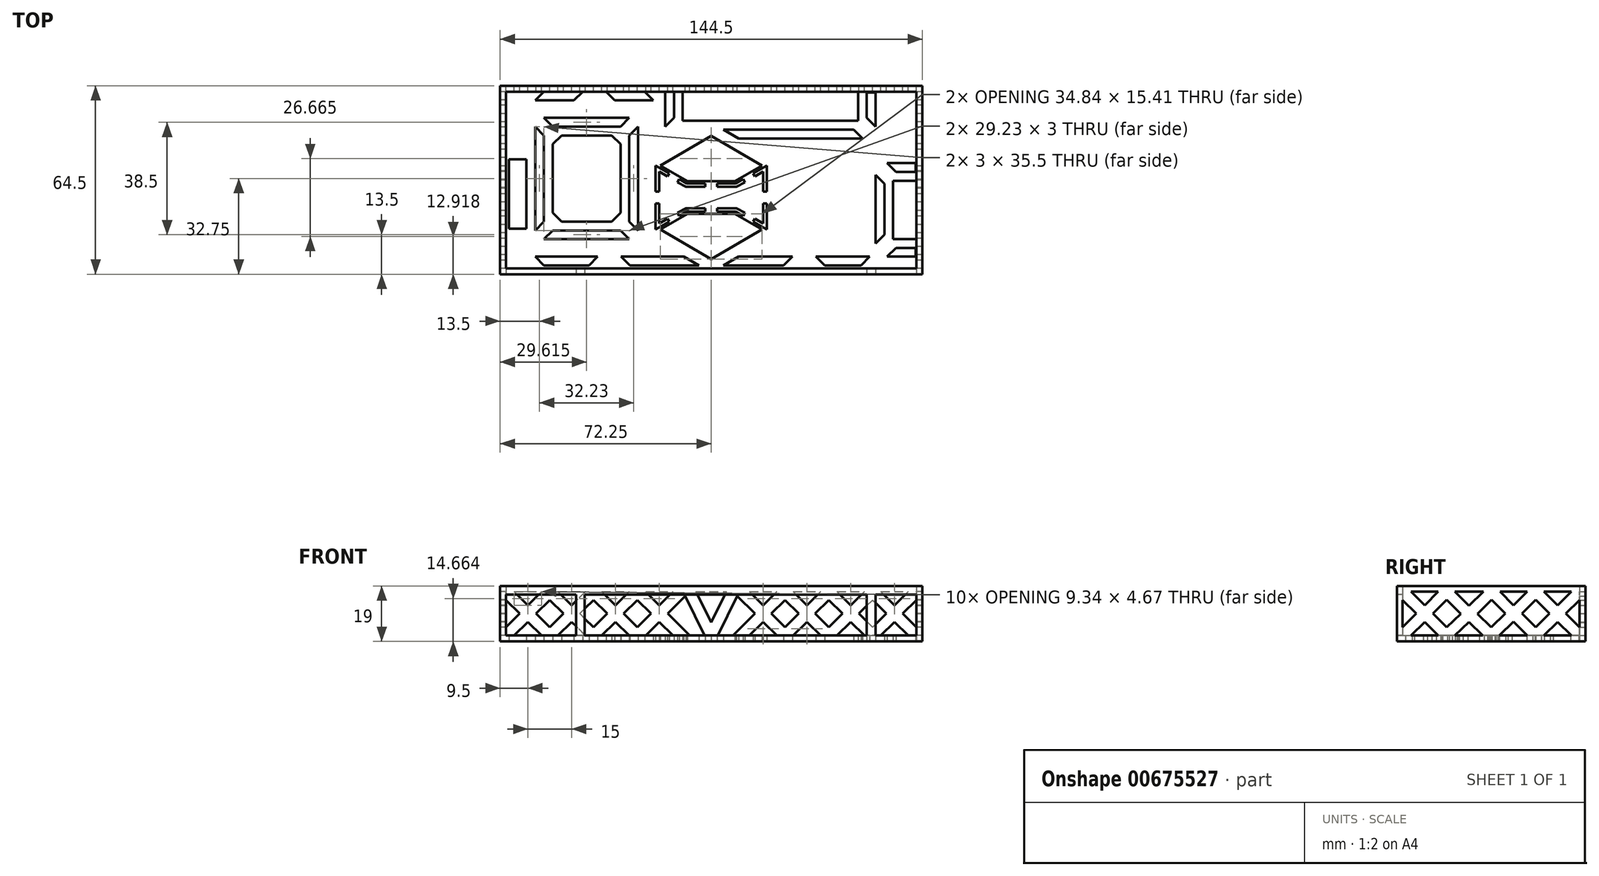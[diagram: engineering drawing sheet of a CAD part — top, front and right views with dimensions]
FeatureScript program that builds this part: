
annotation { "Feature Type Name" : "Feature", "Feature Type Description" : "" }
export const myFeature = defineFeature(function(context is Context, id is Id, definition is map)
    precondition{}
    {
        {
            var Q0;
            Q0=qCreatedBy(makeId("Top.planeOp"),FACE);
            var sketch = newSketch(context, id + "F0", { "sketchPlane" : qUnion([Q0])});
            skLineSegment(sketch, "E0.bottom", {"start": v(-72.25, 32.25) * mm, "end": v(72.25, 32.25) * mm});
            skLineSegment(sketch, "E0.top", {"start": v(-72.25, -32.25) * mm, "end": v(72.25, -32.25) * mm});
            skLineSegment(sketch, "E0.left", {"start": v(-72.25, 32.25) * mm, "end": v(-72.25, -32.25) * mm});
            skLineSegment(sketch, "E0.right", {"start": v(72.25, 32.25) * mm, "end": v(72.25, -32.25) * mm});
            skSolve(sketch);
        }
        {
            var Q0;
            Q0 = qSketchRegion(id + "F0", true);
            extrude(context, id + "F1", {"entities" : qUnion([Q0]), "depth" : 2 * mm, "offsetDistance" : 25 * mm});
        }
        {
            var Q0;
            Q0=makeQuery(id+"F1.opExtrude","CAP_FACE",FACE,{"disambiguationData":[OSD([sQuery(id+"F0.wireOp",EDGE,"E0.bottom"),sQuery(id+"F0.wireOp",EDGE,"E0.top"),sQuery(id+"F0.wireOp",EDGE,"E0.left"),sQuery(id+"F0.wireOp",EDGE,"E0.right")])],"isStart":false});
            var sketch = newSketch(context, id + "F2", { "sketchPlane" : qUnion([Q0])});
            skLineSegment(sketch, "E1.0", {"start": v(-72.25, 32.25) * mm, "end": v(-72.25, -32.25) * mm});
            skLineSegment(sketch, "E1.1", {"start": v(72.25, 32.25) * mm, "end": v(-72.25, 32.25) * mm});
            skLineSegment(sketch, "E1.2", {"start": v(72.25, -32.25) * mm, "end": v(72.25, 32.25) * mm});
            skLineSegment(sketch, "E1.3", {"start": v(-72.25, -32.25) * mm, "end": v(72.25, -32.25) * mm});
            skLineSegment(sketch, "E2.0", {"start": v(-70.25, 30.25) * mm, "end": v(-70.25, -30.25) * mm});
            skLineSegment(sketch, "E2.1", {"start": v(70.25, 30.25) * mm, "end": v(-70.25, 30.25) * mm});
            skLineSegment(sketch, "E2.2", {"start": v(70.25, -30.25) * mm, "end": v(70.25, 30.25) * mm});
            skLineSegment(sketch, "E2.3", {"start": v(-70.25, -30.25) * mm, "end": v(70.25, -30.25) * mm});
            skSolve(sketch);
        }
        {
            var Q0;
            Q0 = qSketchRegion(id + "F2", true);
            extrude(context, id + "F3", {"entities" : qUnion([Q0]), "operationType" : NewBodyOperationType.ADD, "depth" : 17 * mm, "offsetDistance" : 25 * mm});
        }
        {
            var Q0;
            Q0=makeQuery(id+"F3.boolean.opBoolean","MERGE",FACE,{"derivedFrom":[makeQuery(id+"F1.opExtrude","SWEPT_FACE",FACE,{"disambiguationData":[OSD([sQuery(id+"F0.wireOp",EDGE,"E0.top")])]}),makeQuery(id+"F3.opExtrude","SWEPT_FACE",FACE,{"disambiguationData":[OSD([sQuery(id+"F2.wireOp",EDGE,"E1.3")])]})]});
            var sketch = newSketch(context, id + "F4", { "sketchPlane" : qUnion([Q0])});
            skLineSegment(sketch, "E3.0", {"start": v(-70.25, 2) * mm, "end": v(-46.25, 2) * mm});
            skLineSegment(sketch, "E3.1", {"start": v(-70.25, 17) * mm, "end": v(-70.25, 2) * mm});
            skLineSegment(sketch, "E3.2", {"start": v(70.25, 17) * mm, "end": v(56.25, 17) * mm});
            skLineSegment(sketch, "E3.3", {"start": v(70.25, 2) * mm, "end": v(70.25, 17) * mm});
            skLineSegment(sketch, "E4", {"start": v(-46.25, 2) * mm, "end": v(-46.25, 17) * mm});
            skLineSegment(sketch, "E5", {"start": v(-44.25, 2) * mm, "end": v(-44.25, 17) * mm});
            skLineSegment(sketch, "E6", {"start": v(56.25, 2) * mm, "end": v(56.25, 17) * mm});
            skLineSegment(sketch, "E7", {"start": v(54.25, 2) * mm, "end": v(54.25, 17) * mm});
            skLineSegment(sketch, "E8.trimOffspring", {"start": v(54.25, 17) * mm, "end": v(-44.25, 17) * mm});
            skLineSegment(sketch, "E9.trimOffspring", {"start": v(56.25, 2) * mm, "end": v(70.25, 2) * mm});
            skLineSegment(sketch, "E10.trimOffspring", {"start": v(-46.25, 17) * mm, "end": v(-70.25, 17) * mm});
            skLineSegment(sketch, "E11.trimOffspring", {"start": v(-44.25, 2) * mm, "end": v(54.25, 2) * mm});
            skSolve(sketch);
        }
        {
            var Q0;
            Q0 = qSketchRegion(id + "F4", true);
            extrude(context, id + "F5", {"entities" : qUnion([Q0]), "operationType" : NewBodyOperationType.REMOVE, "oppositeDirection" : true, "depth" : 25 * mm, "offsetDistance" : 25 * mm});
        }
        {
            var Q0;
            Q0=makeQuery(id+"F1.opExtrude","CAP_FACE",FACE,{"disambiguationData":[OSD([sQuery(id+"F0.wireOp",EDGE,"E0.bottom"),sQuery(id+"F0.wireOp",EDGE,"E0.top"),sQuery(id+"F0.wireOp",EDGE,"E0.left"),sQuery(id+"F0.wireOp",EDGE,"E0.right")])],"isStart":true});
            var sketch = newSketch(context, id + "F6", { "sketchPlane" : qUnion([Q0])});
            skLineSegment(sketch, "E12.0", {"start": v(-70.25, 30.25) * mm, "end": v(-70.25, -30.25) * mm, "construction": true});
            skLineSegment(sketch, "E12.1", {"start": v(70.25, 30.25) * mm, "end": v(-70.25, 30.25) * mm, "construction": true});
            skLineSegment(sketch, "E12.3", {"start": v(-9.75, -30.25) * mm, "end": v(50.25, -30.25) * mm});
            skLineSegment(sketch, "E13", {"start": v(50.25, -30.25) * mm, "end": v(50.25, -20.25) * mm});
            skLineSegment(sketch, "E14", {"start": v(-9.75, -30.25) * mm, "end": v(-9.75, -20.25) * mm});
            skLineSegment(sketch, "E15", {"start": v(-9.75, -20.25) * mm, "end": v(50.25, -20.25) * mm});
            skLineSegment(sketch, "E16", {"start": v(50.25, -30.25) * mm, "end": v(70.25, -30.25) * mm, "construction": true});
            skLineSegment(sketch, "E17", {"start": v(-9.75, -30.25) * mm, "end": v(-70.25, -30.25) * mm, "construction": true});
            skLineSegment(sketch, "E18", {"start": v(70.25, 20.25) * mm, "end": v(62.25, 20.25) * mm});
            skLineSegment(sketch, "E19", {"start": v(70.25, 0.25) * mm, "end": v(62.25, 0.25) * mm});
            skLineSegment(sketch, "E20", {"start": v(70.25, -30.25) * mm, "end": v(70.25, 0.25) * mm, "construction": true});
            skLineSegment(sketch, "E21", {"start": v(70.25, 20.25) * mm, "end": v(70.25, 30.25) * mm, "construction": true});
            skLineSegment(sketch, "E22", {"start": v(70.25, 20.25) * mm, "end": v(70.25, 0.25) * mm});
            skLineSegment(sketch, "E23", {"start": v(62.25, 0.25) * mm, "end": v(62.25, 20.25) * mm});
            skSolve(sketch);
        }
        {
            var Q0;
            Q0 = qSketchRegion(id + "F6", true);
            extrude(context, id + "F7", {"entities" : qUnion([Q0]), "operationType" : NewBodyOperationType.REMOVE, "oppositeDirection" : true, "depth" : 25 * mm, "offsetDistance" : 25 * mm});
        }
        {
            var Q0;
            Q0=makeQuery(id+"F3.boolean.opBoolean","MERGE",FACE,{"derivedFrom":[makeQuery(id+"F1.opExtrude","SWEPT_FACE",FACE,{"disambiguationData":[OSD([sQuery(id+"F0.wireOp",EDGE,"E0.left")])]}),makeQuery(id+"F3.opExtrude","SWEPT_FACE",FACE,{"disambiguationData":[OSD([sQuery(id+"F2.wireOp",EDGE,"E1.0")])]})]});
            var sketch = newSketch(context, id + "F8", { "sketchPlane" : qUnion([Q0])});
            skLineSegment(sketch, "E24.0", {"start": v(-27.42, 2) * mm, "end": v(-18.08, 2) * mm});
            skLineSegment(sketch, "E24.1", {"start": v(-30.25, 14.17) * mm, "end": v(-30.25, 4.83) * mm});
            skLineSegment(sketch, "E24.3", {"start": v(30.25, 4.83) * mm, "end": v(30.25, 14.17) * mm});
            skLineSegment(sketch, "E25", {"start": v(-27.42, 17) * mm, "end": v(-18.08, 17) * mm});
            skLineSegment(sketch, "E26", {"start": v(-12.4, 17) * mm, "end": v(-3.08, 17) * mm});
            skLineSegment(sketch, "E27", {"start": v(2.63, 17) * mm, "end": v(12.4, 17) * mm});
            skLineSegment(sketch, "E28", {"start": v(18.08, 17) * mm, "end": v(27.42, 17) * mm});
            skLineSegment(sketch, "E29", {"start": v(-30.25, 2) * mm, "end": v(-15.25, 17) * mm, "construction": true});
            skLineSegment(sketch, "E30", {"start": v(-15.25, 17) * mm, "end": v(0, 2) * mm, "construction": true});
            skLineSegment(sketch, "E31", {"start": v(0, 2) * mm, "end": v(15.25, 17) * mm, "construction": true});
            skLineSegment(sketch, "E32", {"start": v(15.25, 17) * mm, "end": v(30.25, 2) * mm, "construction": true});
            skLineSegment(sketch, "E33", {"start": v(15.25, 17) * mm, "end": v(15.25, 2) * mm, "construction": true});
            skLineSegment(sketch, "E34", {"start": v(-0.25, 17) * mm, "end": v(0, 2) * mm, "construction": true});
            skLineSegment(sketch, "E35", {"start": v(-15.25, 17) * mm, "end": v(-15.25, 2) * mm, "construction": true});
            skLineSegment(sketch, "E36", {"start": v(-30.25, 17) * mm, "end": v(-15.25, 2) * mm, "construction": true});
            skLineSegment(sketch, "E37", {"start": v(-0.25, 17) * mm, "end": v(-15.25, 2) * mm, "construction": true});
            skLineSegment(sketch, "E38", {"start": v(30.25, 17) * mm, "end": v(15.25, 2) * mm, "construction": true});
            skLineSegment(sketch, "E39", {"start": v(-0.25, 17) * mm, "end": v(15.25, 2) * mm, "construction": true});
            skLineSegment(sketch, "E40.0", {"start": v(-27.42, 17) * mm, "end": v(-22.75, 12.33) * mm});
            skLineSegment(sketch, "E40.1", {"start": v(-3.08, 17) * mm, "end": v(-7.7, 12.38) * mm});
            skLineSegment(sketch, "E40.2", {"start": v(2.63, 17) * mm, "end": v(7.55, 12.23) * mm});
            skLineSegment(sketch, "E40.3", {"start": v(27.42, 17) * mm, "end": v(22.75, 12.33) * mm});
            skLineSegment(sketch, "E41.0", {"start": v(-30.25, 14.17) * mm, "end": v(-25.58, 9.5) * mm});
            skLineSegment(sketch, "E41.1", {"start": v(-0.23, 14.2) * mm, "end": v(-4.85, 9.57) * mm});
            skLineSegment(sketch, "E41.2", {"start": v(-0.23, 14.2) * mm, "end": v(4.7, 9.43) * mm});
            skLineSegment(sketch, "E41.3", {"start": v(30.25, 14.17) * mm, "end": v(18.08, 2) * mm});
            skLineSegment(sketch, "E42.0", {"start": v(15.24, 14.18) * mm, "end": v(19.92, 9.5) * mm});
            skLineSegment(sketch, "E42.1", {"start": v(2.85, 2) * mm, "end": v(7.57, 6.64) * mm});
            skLineSegment(sketch, "E42.2", {"start": v(-15.24, 14.18) * mm, "end": v(-10.53, 9.55) * mm});
            skLineSegment(sketch, "E42.3", {"start": v(-27.42, 2) * mm, "end": v(-22.75, 6.67) * mm});
            skLineSegment(sketch, "E43.0", {"start": v(18.08, 17) * mm, "end": v(22.75, 12.33) * mm});
            skLineSegment(sketch, "E43.1", {"start": v(0, 4.8) * mm, "end": v(4.7, 9.43) * mm});
            skLineSegment(sketch, "E43.2", {"start": v(-12.4, 17) * mm, "end": v(-7.7, 12.38) * mm});
            skLineSegment(sketch, "E43.3", {"start": v(-30.25, 4.83) * mm, "end": v(-25.58, 9.5) * mm});
            skLineSegment(sketch, "E44.trimOffspring", {"start": v(7.55, 12.23) * mm, "end": v(12.4, 17) * mm});
            skLineSegment(sketch, "E45.trimOffspring", {"start": v(7.57, 6.64) * mm, "end": v(12.37, 2) * mm});
            skLineSegment(sketch, "E46.trimOffspring", {"start": v(10.43, 9.45) * mm, "end": v(15.23, 4.8) * mm});
            skLineSegment(sketch, "E47.trimOffspring", {"start": v(22.75, 6.67) * mm, "end": v(27.42, 2) * mm});
            skLineSegment(sketch, "E48.trimOffspring", {"start": v(19.92, 9.5) * mm, "end": v(15.23, 4.8) * mm});
            skLineSegment(sketch, "E49.trimOffspring", {"start": v(25.58, 9.5) * mm, "end": v(30.25, 4.83) * mm});
            skLineSegment(sketch, "E50.trimOffspring", {"start": v(10.43, 9.45) * mm, "end": v(15.24, 14.18) * mm});
            skLineSegment(sketch, "E51.trimOffspring", {"start": v(-7.68, 6.75) * mm, "end": v(-2.85, 2) * mm});
            skLineSegment(sketch, "E52.trimOffspring", {"start": v(-7.68, 6.75) * mm, "end": v(-12.42, 2) * mm});
            skLineSegment(sketch, "E53.trimOffspring", {"start": v(-4.85, 9.57) * mm, "end": v(0, 4.8) * mm});
            skLineSegment(sketch, "E54.trimOffspring", {"start": v(-10.53, 9.55) * mm, "end": v(-15.25, 4.83) * mm});
            skLineSegment(sketch, "E55.trimOffspring", {"start": v(-19.92, 9.5) * mm, "end": v(-15.25, 4.83) * mm});
            skLineSegment(sketch, "E56.trimOffspring", {"start": v(-22.75, 12.33) * mm, "end": v(-18.08, 17) * mm});
            skLineSegment(sketch, "E57.trimOffspring", {"start": v(-22.75, 6.67) * mm, "end": v(-18.08, 2) * mm});
            skLineSegment(sketch, "E58.trimOffspring", {"start": v(-19.92, 9.5) * mm, "end": v(-15.24, 14.18) * mm});
            skLineSegment(sketch, "E59.trimOffspring", {"start": v(-12.42, 2) * mm, "end": v(-2.85, 2) * mm});
            skLineSegment(sketch, "E60.trimOffspring", {"start": v(2.85, 2) * mm, "end": v(12.37, 2) * mm});
            skLineSegment(sketch, "E61.trimOffspring", {"start": v(18.08, 2) * mm, "end": v(27.42, 2) * mm});
            skSolve(sketch);
        }
        {
            var Q0;
            Q0 = qSketchRegion(id + "F8", true);
            extrude(context, id + "F9", {"entities" : qUnion([Q0]), "operationType" : NewBodyOperationType.REMOVE, "endBound" : BoundingType.THROUGH_ALL, "oppositeDirection" : true, "depth" : 25 * mm, "offsetDistance" : 25 * mm});
        }
        {
            var Q0;
            Q0=makeQuery(id+"F3.boolean.opBoolean","MERGE",FACE,{"derivedFrom":[makeQuery(id+"F1.opExtrude","SWEPT_FACE",FACE,{"disambiguationData":[OSD([sQuery(id+"F0.wireOp",EDGE,"E0.bottom")])]}),makeQuery(id+"F3.opExtrude","SWEPT_FACE",FACE,{"disambiguationData":[OSD([sQuery(id+"F2.wireOp",EDGE,"E1.1")])]})]});
            var sketch = newSketch(context, id + "F10", { "sketchPlane" : qUnion([Q0])});
            skLineSegment(sketch, "E62.0", {"start": v(-67.42, 2) * mm, "end": v(-58.08, 2) * mm});
            skLineSegment(sketch, "E62.1", {"start": v(-70.25, 14.17) * mm, "end": v(-70.25, 4.83) * mm});
            skLineSegment(sketch, "E62.2", {"start": v(67.42, 17) * mm, "end": v(58.08, 17) * mm});
            skLineSegment(sketch, "E62.3", {"start": v(70.25, 4.83) * mm, "end": v(70.25, 14.17) * mm});
            skLineSegment(sketch, "E63", {"start": v(0, 17) * mm, "end": v(0, 2) * mm, "construction": true});
            skLineSegment(sketch, "E64", {"start": v(-70.25, 17) * mm, "end": v(-55.25, 2) * mm, "construction": true});
            skLineSegment(sketch, "E65", {"start": v(-55.25, 2) * mm, "end": v(-40.25, 17) * mm, "construction": true});
            skLineSegment(sketch, "E66", {"start": v(-40.25, 17) * mm, "end": v(-25.25, 2) * mm, "construction": true});
            skLineSegment(sketch, "E67", {"start": v(-25.25, 2) * mm, "end": v(-10.25, 17) * mm, "construction": true});
            skLineSegment(sketch, "E68", {"start": v(70.25, 17) * mm, "end": v(55.25, 2) * mm, "construction": true});
            skLineSegment(sketch, "E69", {"start": v(55.25, 2) * mm, "end": v(40.25, 17) * mm, "construction": true});
            skLineSegment(sketch, "E70", {"start": v(40.25, 17) * mm, "end": v(25.25, 2) * mm, "construction": true});
            skLineSegment(sketch, "E71", {"start": v(25.25, 2) * mm, "end": v(10.25, 17) * mm, "construction": true});
            skLineSegment(sketch, "E72", {"start": v(-70.25, 2) * mm, "end": v(-55.25, 17) * mm, "construction": true});
            skLineSegment(sketch, "E73", {"start": v(-55.25, 17) * mm, "end": v(-40.25, 2) * mm, "construction": true});
            skLineSegment(sketch, "E74", {"start": v(-40.25, 2) * mm, "end": v(-25.25, 17) * mm, "construction": true});
            skLineSegment(sketch, "E75", {"start": v(-25.25, 17) * mm, "end": v(-10.25, 2) * mm, "construction": true});
            skLineSegment(sketch, "E76", {"start": v(70.25, 2) * mm, "end": v(55.25, 17) * mm, "construction": true});
            skLineSegment(sketch, "E77", {"start": v(55.25, 17) * mm, "end": v(40.25, 2) * mm, "construction": true});
            skLineSegment(sketch, "E78", {"start": v(40.25, 2) * mm, "end": v(25.25, 17) * mm, "construction": true});
            skLineSegment(sketch, "E79", {"start": v(25.25, 17) * mm, "end": v(10.25, 2) * mm, "construction": true});
            skLineSegment(sketch, "E80.0", {"start": v(-22.42, 2) * mm, "end": v(-17.75, 6.67) * mm});
            skLineSegment(sketch, "E80.1", {"start": v(-40.25, 14.17) * mm, "end": v(-35.58, 9.5) * mm});
            skLineSegment(sketch, "E80.2", {"start": v(-52.42, 2) * mm, "end": v(-47.75, 6.67) * mm});
            skLineSegment(sketch, "E80.3", {"start": v(-70.25, 14.17) * mm, "end": v(-65.58, 9.5) * mm});
            skLineSegment(sketch, "E81.0", {"start": v(-25.25, 4.83) * mm, "end": v(-20.58, 9.5) * mm});
            skLineSegment(sketch, "E81.1", {"start": v(-37.42, 17) * mm, "end": v(-32.75, 12.33) * mm});
            skLineSegment(sketch, "E81.2", {"start": v(-55.25, 4.83) * mm, "end": v(-50.58, 9.5) * mm});
            skLineSegment(sketch, "E81.3", {"start": v(-67.42, 17) * mm, "end": v(-62.75, 12.33) * mm});
            skLineSegment(sketch, "E82.0", {"start": v(-25.25, 14.17) * mm, "end": v(-20.58, 9.5) * mm});
            skLineSegment(sketch, "E82.1", {"start": v(-37.42, 2) * mm, "end": v(-25.25, 14.17) * mm});
            skLineSegment(sketch, "E82.2", {"start": v(-55.25, 14.17) * mm, "end": v(-50.58, 9.5) * mm});
            skLineSegment(sketch, "E82.3", {"start": v(-67.42, 2) * mm, "end": v(-62.75, 6.67) * mm});
            skLineSegment(sketch, "E83.0", {"start": v(-22.42, 17) * mm, "end": v(-17.75, 12.33) * mm});
            skLineSegment(sketch, "E83.1", {"start": v(-40.25, 4.83) * mm, "end": v(-35.58, 9.5) * mm});
            skLineSegment(sketch, "E83.2", {"start": v(-52.42, 17) * mm, "end": v(-47.75, 12.33) * mm});
            skLineSegment(sketch, "E83.3", {"start": v(-70.25, 4.83) * mm, "end": v(-65.58, 9.5) * mm});
            skLineSegment(sketch, "E84.0", {"start": v(25.25, 4.83) * mm, "end": v(20.58, 9.5) * mm});
            skLineSegment(sketch, "E84.1", {"start": v(37.42, 17) * mm, "end": v(32.75, 12.33) * mm});
            skLineSegment(sketch, "E84.2", {"start": v(55.25, 4.83) * mm, "end": v(50.58, 9.5) * mm});
            skLineSegment(sketch, "E84.3", {"start": v(67.42, 17) * mm, "end": v(62.75, 12.33) * mm});
            skLineSegment(sketch, "E85.0", {"start": v(22.42, 2) * mm, "end": v(17.75, 6.67) * mm});
            skLineSegment(sketch, "E85.1", {"start": v(40.25, 14.17) * mm, "end": v(35.58, 9.5) * mm});
            skLineSegment(sketch, "E85.2", {"start": v(52.42, 2) * mm, "end": v(47.75, 6.67) * mm});
            skLineSegment(sketch, "E85.3", {"start": v(70.25, 14.17) * mm, "end": v(65.58, 9.5) * mm});
            skLineSegment(sketch, "E86.0", {"start": v(22.42, 17) * mm, "end": v(17.75, 12.33) * mm});
            skLineSegment(sketch, "E86.1", {"start": v(40.25, 4.83) * mm, "end": v(35.58, 9.5) * mm});
            skLineSegment(sketch, "E86.2", {"start": v(52.42, 17) * mm, "end": v(47.75, 12.33) * mm});
            skLineSegment(sketch, "E86.3", {"start": v(70.25, 4.83) * mm, "end": v(65.58, 9.5) * mm});
            skLineSegment(sketch, "E87.0", {"start": v(25.25, 14.17) * mm, "end": v(20.58, 9.5) * mm});
            skLineSegment(sketch, "E87.1", {"start": v(37.42, 2) * mm, "end": v(32.75, 6.67) * mm});
            skLineSegment(sketch, "E87.2", {"start": v(55.25, 14.17) * mm, "end": v(50.58, 9.5) * mm});
            skLineSegment(sketch, "E87.3", {"start": v(67.42, 2) * mm, "end": v(62.75, 6.67) * mm});
            skLineSegment(sketch, "E88.trimOffspring", {"start": v(-19.16, 8.09) * mm, "end": v(-13.08, 2) * mm});
            skLineSegment(sketch, "E89.trimOffspring", {"start": v(-17.75, 12.33) * mm, "end": v(-13.08, 17) * mm});
            skLineSegment(sketch, "E90.trimOffspring", {"start": v(-14.92, 9.5) * mm, "end": v(-7.42, 2) * mm});
            skLineSegment(sketch, "E91.trimOffspring", {"start": v(-14.92, 9.5) * mm, "end": v(-8.91, 15.5) * mm});
            skLineSegment(sketch, "E92.trimOffspring", {"start": v(-32.75, 6.67) * mm, "end": v(-28.08, 2) * mm});
            skLineSegment(sketch, "E93.trimOffspring", {"start": v(-32.75, 12.33) * mm, "end": v(-28.08, 17) * mm});
            skLineSegment(sketch, "E94.trimOffspring", {"start": v(-29.92, 9.5) * mm, "end": v(-25.25, 4.83) * mm});
            skLineSegment(sketch, "E95.trimOffspring", {"start": v(-47.75, 6.67) * mm, "end": v(-43.08, 2) * mm});
            skLineSegment(sketch, "E96.trimOffspring", {"start": v(-47.75, 12.33) * mm, "end": v(-43.08, 17) * mm});
            skLineSegment(sketch, "E97.trimOffspring", {"start": v(-44.92, 9.5) * mm, "end": v(-40.25, 4.83) * mm});
            skLineSegment(sketch, "E98.trimOffspring", {"start": v(-44.92, 9.5) * mm, "end": v(-40.25, 14.17) * mm});
            skLineSegment(sketch, "E99.trimOffspring", {"start": v(-59.92, 9.5) * mm, "end": v(-55.25, 4.83) * mm});
            skLineSegment(sketch, "E100.trimOffspring", {"start": v(-59.92, 9.5) * mm, "end": v(-55.25, 14.17) * mm});
            skLineSegment(sketch, "E101.trimOffspring", {"start": v(-62.75, 6.67) * mm, "end": v(-58.08, 2) * mm});
            skLineSegment(sketch, "E102.trimOffspring", {"start": v(-62.75, 12.33) * mm, "end": v(-58.08, 17) * mm});
            skLineSegment(sketch, "E103.trimOffspring", {"start": v(14.92, 9.5) * mm, "end": v(8.91, 15.5) * mm});
            skLineSegment(sketch, "E104.trimOffspring", {"start": v(17.75, 6.67) * mm, "end": v(13.08, 2) * mm});
            skLineSegment(sketch, "E105.trimOffspring", {"start": v(17.75, 12.33) * mm, "end": v(13.08, 17) * mm});
            skLineSegment(sketch, "E106.trimOffspring", {"start": v(14.92, 9.5) * mm, "end": v(7.42, 2) * mm});
            skLineSegment(sketch, "E107.trimOffspring", {"start": v(29.92, 9.5) * mm, "end": v(25.25, 14.17) * mm});
            skLineSegment(sketch, "E108.trimOffspring", {"start": v(32.75, 6.67) * mm, "end": v(28.08, 2) * mm});
            skLineSegment(sketch, "E109.trimOffspring", {"start": v(32.75, 12.33) * mm, "end": v(28.08, 17) * mm});
            skLineSegment(sketch, "E110.trimOffspring", {"start": v(29.92, 9.5) * mm, "end": v(25.25, 4.83) * mm});
            skLineSegment(sketch, "E111.trimOffspring", {"start": v(44.92, 9.5) * mm, "end": v(40.25, 14.17) * mm});
            skLineSegment(sketch, "E112.trimOffspring", {"start": v(47.75, 6.67) * mm, "end": v(43.08, 2) * mm});
            skLineSegment(sketch, "E113.trimOffspring", {"start": v(47.75, 12.33) * mm, "end": v(43.08, 17) * mm});
            skLineSegment(sketch, "E114.trimOffspring", {"start": v(44.92, 9.5) * mm, "end": v(40.25, 4.83) * mm});
            skLineSegment(sketch, "E115.trimOffspring", {"start": v(59.92, 9.5) * mm, "end": v(55.25, 4.83) * mm});
            skLineSegment(sketch, "E116.trimOffspring", {"start": v(62.75, 12.33) * mm, "end": v(58.08, 17) * mm});
            skLineSegment(sketch, "E117.trimOffspring", {"start": v(62.75, 6.67) * mm, "end": v(58.08, 2) * mm});
            skLineSegment(sketch, "E118.trimOffspring", {"start": v(59.92, 9.5) * mm, "end": v(55.25, 14.17) * mm});
            skLineSegment(sketch, "E119.trimOffspring", {"start": v(28.08, 2) * mm, "end": v(37.42, 2) * mm});
            skLineSegment(sketch, "E120.trimOffspring", {"start": v(13.08, 2) * mm, "end": v(22.42, 2) * mm});
            skLineSegment(sketch, "E121.trimOffspring", {"start": v(5.2, 17) * mm, "end": v(-5.2, 17) * mm});
            skLineSegment(sketch, "E122.trimOffspring", {"start": v(22.42, 17) * mm, "end": v(13.08, 17) * mm});
            skLineSegment(sketch, "E123.trimOffspring", {"start": v(37.42, 17) * mm, "end": v(28.08, 17) * mm});
            skLineSegment(sketch, "E124.trimOffspring", {"start": v(43.08, 2) * mm, "end": v(52.42, 2) * mm});
            skLineSegment(sketch, "E125.trimOffspring", {"start": v(58.08, 2) * mm, "end": v(67.42, 2) * mm});
            skLineSegment(sketch, "E126.trimOffspring", {"start": v(52.42, 17) * mm, "end": v(43.08, 17) * mm});
            skLineSegment(sketch, "E127.trimOffspring", {"start": v(-7.42, 2) * mm, "end": v(-2.23, 2) * mm});
            skLineSegment(sketch, "E128.trimOffspring", {"start": v(-22.42, 2) * mm, "end": v(-13.08, 2) * mm});
            skLineSegment(sketch, "E129.trimOffspring", {"start": v(-37.42, 2) * mm, "end": v(-28.08, 2) * mm});
            skLineSegment(sketch, "E130.trimOffspring", {"start": v(-52.42, 2) * mm, "end": v(-43.08, 2) * mm});
            skLineSegment(sketch, "E131.trimOffspring", {"start": v(-58.08, 17) * mm, "end": v(-67.42, 17) * mm});
            skLineSegment(sketch, "E132.trimOffspring", {"start": v(-43.08, 17) * mm, "end": v(-52.42, 17) * mm});
            skLineSegment(sketch, "E133.trimOffspring", {"start": v(-28.08, 17) * mm, "end": v(-37.42, 17) * mm});
            skLineSegment(sketch, "E134.trimOffspring", {"start": v(-13.08, 17) * mm, "end": v(-22.42, 17) * mm});
            skLineSegment(sketch, "E135", {"start": v(-7.42, 17) * mm, "end": v(0, 2) * mm, "construction": true});
            skLineSegment(sketch, "E136", {"start": v(7.42, 17) * mm, "end": v(0, 2) * mm, "construction": true});
            skLineSegment(sketch, "E137.0", {"start": v(5.2, 17) * mm, "end": v(0, 6.5) * mm});
            skLineSegment(sketch, "E137.1", {"start": v(-5.2, 17) * mm, "end": v(0, 6.5) * mm});
            skLineSegment(sketch, "E138.0", {"start": v(8.91, 15.5) * mm, "end": v(2.23, 2) * mm});
            skLineSegment(sketch, "E138.1", {"start": v(-8.91, 15.5) * mm, "end": v(-2.23, 2) * mm});
            skLineSegment(sketch, "E139.trimOffspring", {"start": v(2.23, 2) * mm, "end": v(7.42, 2) * mm});
            skSolve(sketch);
        }
        {
            var Q0;
            Q0 = qSketchRegion(id + "F10", true);
            extrude(context, id + "F11", {"entities" : qUnion([Q0]), "operationType" : NewBodyOperationType.REMOVE, "oppositeDirection" : true, "depth" : 25 * mm, "offsetDistance" : 25 * mm});
        }
        {
            var Q0;
            {var subQ0=sQuery(id+"F0.wireOp",EDGE,"E0.top");var subQ1=sQuery(id+"F0.wireOp",EDGE,"E0.right");var subQ2=sQuery(id+"F0.wireOp",EDGE,"E0.bottom");var subQ3=sQuery(id+"F0.wireOp",EDGE,"E0.left");Q0=makeQuery(id+"FJUS3B1TuTwB0FU_1.boolean.opBoolean","SPLIT",FACE,{"disambiguationData":[TD([makeQuery(id+"F1.opExtrude","SWEPT_FACE",FACE,{"disambiguationData":[OSD([subQ2])]})])],"derivedFrom":makeQuery(id+"F1.opExtrude","CAP_FACE",FACE,{"disambiguationData":[OSD([subQ2,subQ0,subQ3,subQ1])],"isStart":true})});}
            var sketch = newSketch(context, id + "F12", { "sketchPlane" : qUnion([Q0])});
            skLineSegment(sketch, "E140.1", {"start": v(9.5, 11.5) * mm, "end": v(9.5, 0.5) * mm});
            skLineSegment(sketch, "E140.4", {"start": v(-9.5, 0.5) * mm, "end": v(-9.5, 11.5) * mm});
            skLineSegment(sketch, "E141", {"start": v(-9.5, 11.5) * mm, "end": v(-4.18, 8.41) * mm});
            skLineSegment(sketch, "E142", {"start": v(9.5, 11.5) * mm, "end": v(4.18, 8.41) * mm});
            skLineSegment(sketch, "E143", {"start": v(-4.18, 3.59) * mm, "end": v(-9.5, 0.5) * mm});
            skLineSegment(sketch, "E144", {"start": v(4.18, 3.59) * mm, "end": v(9.5, 0.5) * mm});
            skLineSegment(sketch, "E145", {"start": v(-4.18, 3.59) * mm, "end": v(4.18, 3.59) * mm});
            skLineSegment(sketch, "E146", {"start": v(4.18, 8.41) * mm, "end": v(-4.18, 8.41) * mm});
            skLineSegment(sketch, "E147.0", {"start": v(4.07, 8.81) * mm, "end": v(-4.07, 8.81) * mm});
            skLineSegment(sketch, "E147.1", {"start": v(-8.7, 11.5) * mm, "end": v(-4.07, 8.81) * mm});
            skLineSegment(sketch, "E147.2", {"start": v(8.7, 11.5) * mm, "end": v(4.07, 8.81) * mm});
            skLineSegment(sketch, "E147.3", {"start": v(0, 16.52) * mm, "end": v(8.7, 11.5) * mm});
            skLineSegment(sketch, "E147.4", {"start": v(-8.7, 11.5) * mm, "end": v(0, 16.52) * mm});
            skLineSegment(sketch, "E148.0", {"start": v(0, -4.52) * mm, "end": v(-8.7, 0.5) * mm});
            skLineSegment(sketch, "E148.1", {"start": v(-4.07, 3.19) * mm, "end": v(-8.7, 0.5) * mm});
            skLineSegment(sketch, "E148.2", {"start": v(8.7, 0.5) * mm, "end": v(0, -4.52) * mm});
            skLineSegment(sketch, "E148.3", {"start": v(4.07, 3.19) * mm, "end": v(8.7, 0.5) * mm});
            skLineSegment(sketch, "E148.4", {"start": v(-4.07, 3.19) * mm, "end": v(4.07, 3.19) * mm});
            skLineSegment(sketch, "E149.0", {"start": v(-8.9, 1.55) * mm, "end": v(-8.9, 10.45) * mm});
            skLineSegment(sketch, "E149.1", {"start": v(-4.34, 4.19) * mm, "end": v(-8.9, 1.55) * mm});
            skLineSegment(sketch, "E149.2", {"start": v(-8.9, 10.45) * mm, "end": v(-4.34, 7.81) * mm});
            skLineSegment(sketch, "E149.3", {"start": v(-4.34, 4.19) * mm, "end": v(4.34, 4.19) * mm});
            skLineSegment(sketch, "E149.4", {"start": v(4.34, 7.81) * mm, "end": v(-4.34, 7.81) * mm});
            skLineSegment(sketch, "E149.5", {"start": v(8.9, 10.45) * mm, "end": v(4.34, 7.81) * mm});
            skLineSegment(sketch, "E149.6", {"start": v(8.9, 10.45) * mm, "end": v(8.9, 1.55) * mm});
            skLineSegment(sketch, "E149.7", {"start": v(4.34, 4.19) * mm, "end": v(8.9, 1.55) * mm});
            skLineSegment(sketch, "E150", {"start": v(9.5, 6) * mm, "end": v(8.9, 6) * mm, "construction": true});
            skLineSegment(sketch, "E151", {"start": v(8.9, 6) * mm, "end": v(-8.9, 6) * mm, "construction": true});
            skLineSegment(sketch, "E152", {"start": v(-8.9, 6) * mm, "end": v(-9.5, 6) * mm, "construction": true});
            skLineSegment(sketch, "E153", {"start": v(0, 16.52) * mm, "end": v(0, 8.81) * mm, "construction": true});
            skLineSegment(sketch, "E154", {"start": v(0, 8.81) * mm, "end": v(0, 8.41) * mm, "construction": true});
            skLineSegment(sketch, "E155", {"start": v(0, 8.41) * mm, "end": v(0, 7.81) * mm, "construction": true});
            skLineSegment(sketch, "E156", {"start": v(0, 7.81) * mm, "end": v(0, 4.19) * mm, "construction": true});
            skLineSegment(sketch, "E157", {"start": v(0, 4.19) * mm, "end": v(0, 3.59) * mm, "construction": true});
            skLineSegment(sketch, "E158", {"start": v(0, 3.59) * mm, "end": v(0, 3.19) * mm, "construction": true});
            skLineSegment(sketch, "E159", {"start": v(0, 3.19) * mm, "end": v(0, -4.52) * mm, "construction": true});
            skSolve(sketch);
        }
        {
            var Q0;
            Q0 = qSketchRegion(id + "F12", true);
            extrude(context, id + "F13", {"entities" : qUnion([Q0]), "depth" : 1 * mm, "offsetDistance" : 25 * mm});
        }
        {
            var Q0;
            Q0=makeQuery(id+"F13.opExtrude","CAP_FACE",FACE,{"disambiguationData":[OSD([sQuery(id+"F12.wireOp",EDGE,"E140.1"),sQuery(id+"F12.wireOp",EDGE,"E140.4"),sQuery(id+"F12.wireOp",EDGE,"E141"),sQuery(id+"F12.wireOp",EDGE,"E142"),sQuery(id+"F12.wireOp",EDGE,"E143"),sQuery(id+"F12.wireOp",EDGE,"E144"),sQuery(id+"F12.wireOp",EDGE,"E145"),sQuery(id+"F12.wireOp",EDGE,"E146"),sQuery(id+"F12.wireOp",EDGE,"E149.0"),sQuery(id+"F12.wireOp",EDGE,"E149.1"),sQuery(id+"F12.wireOp",EDGE,"E149.2"),sQuery(id+"F12.wireOp",EDGE,"E149.3"),sQuery(id+"F12.wireOp",EDGE,"E149.4"),sQuery(id+"F12.wireOp",EDGE,"E149.5"),sQuery(id+"F12.wireOp",EDGE,"E149.6"),sQuery(id+"F12.wireOp",EDGE,"E149.7")])],"isStart":false});
            var sketch = newSketch(context, id + "F14", { "sketchPlane" : qUnion([Q0])});
            skPoint(sketch, "E160", {"position": v(0, 6) * mm});
            skSolve(sketch);
        }
        {
            var Q0;
            Q0=makeQuery(id+"F13.opExtrude","SWEPT_BODY",BODY,{"disambiguationData":[OSD([sQuery(id+"F12.wireOp",EDGE,"E140.1"),sQuery(id+"F12.wireOp",EDGE,"E140.4"),sQuery(id+"F12.wireOp",EDGE,"E141"),sQuery(id+"F12.wireOp",EDGE,"E142"),sQuery(id+"F12.wireOp",EDGE,"E143"),sQuery(id+"F12.wireOp",EDGE,"E144"),sQuery(id+"F12.wireOp",EDGE,"E145"),sQuery(id+"F12.wireOp",EDGE,"E146"),sQuery(id+"F12.wireOp",EDGE,"E149.0"),sQuery(id+"F12.wireOp",EDGE,"E149.1"),sQuery(id+"F12.wireOp",EDGE,"E149.2"),sQuery(id+"F12.wireOp",EDGE,"E149.3"),sQuery(id+"F12.wireOp",EDGE,"E149.4"),sQuery(id+"F12.wireOp",EDGE,"E149.5"),sQuery(id+"F12.wireOp",EDGE,"E149.6"),sQuery(id+"F12.wireOp",EDGE,"E149.7")])]});
            var Q1;
            Q1=makeQuery(id+"F13.opExtrude","SWEPT_BODY",BODY,{"disambiguationData":[OSD([sQuery(id+"F12.wireOp",EDGE,"E147.0"),sQuery(id+"F12.wireOp",EDGE,"E147.1"),sQuery(id+"F12.wireOp",EDGE,"E147.2"),sQuery(id+"F12.wireOp",EDGE,"E147.3"),sQuery(id+"F12.wireOp",EDGE,"E147.4")])]});
            var Q2;
            Q2=makeQuery(id+"F13.opExtrude","SWEPT_BODY",BODY,{"disambiguationData":[OSD([sQuery(id+"F12.wireOp",EDGE,"E148.0"),sQuery(id+"F12.wireOp",EDGE,"E148.1"),sQuery(id+"F12.wireOp",EDGE,"E148.2"),sQuery(id+"F12.wireOp",EDGE,"E148.3"),sQuery(id+"F12.wireOp",EDGE,"E148.4")])]});
            var Q3;
            Q3=sQuery(id+"F14.wireOp",VERTEX,"E160");
            transform(context, id + "F15", {"entities" : qUnion([Q0, Q1, Q2]), "transformType" : TransformType.SCALE_UNIFORMLY, "scale" : 2, "scalePoint" : qUnion([Q3]), "makeCopy" : false});
        }
        {
            var Q0;
            Q0=makeQuery(id+"F13.opExtrude","CAP_FACE",FACE,{"disambiguationData":[OSD([sQuery(id+"F12.wireOp",EDGE,"E140.1"),sQuery(id+"F12.wireOp",EDGE,"E140.4"),sQuery(id+"F12.wireOp",EDGE,"E141"),sQuery(id+"F12.wireOp",EDGE,"E142"),sQuery(id+"F12.wireOp",EDGE,"E143"),sQuery(id+"F12.wireOp",EDGE,"E144"),sQuery(id+"F12.wireOp",EDGE,"E145"),sQuery(id+"F12.wireOp",EDGE,"E146"),sQuery(id+"F12.wireOp",EDGE,"E149.0"),sQuery(id+"F12.wireOp",EDGE,"E149.1"),sQuery(id+"F12.wireOp",EDGE,"E149.2"),sQuery(id+"F12.wireOp",EDGE,"E149.3"),sQuery(id+"F12.wireOp",EDGE,"E149.4"),sQuery(id+"F12.wireOp",EDGE,"E149.5"),sQuery(id+"F12.wireOp",EDGE,"E149.6"),sQuery(id+"F12.wireOp",EDGE,"E149.7")])],"isStart":false});
            var sketch = newSketch(context, id + "F16", { "sketchPlane" : qUnion([Q0])});
            skLineSegment(sketch, "E161.0", {"start": v(-8.36, 10.83) * mm, "end": v(-19.02, 16.98) * mm});
            skLineSegment(sketch, "E161.1", {"start": v(8.36, 10.83) * mm, "end": v(-8.36, 10.83) * mm});
            skLineSegment(sketch, "E161.2", {"start": v(-19.02, 16.98) * mm, "end": v(-19.02, -4.98) * mm});
            skLineSegment(sketch, "E161.3", {"start": v(19.02, 16.98) * mm, "end": v(8.36, 10.83) * mm});
            skLineSegment(sketch, "E161.4", {"start": v(-19.02, -4.98) * mm, "end": v(-8.36, 1.17) * mm});
            skLineSegment(sketch, "E161.5", {"start": v(-8.36, 1.17) * mm, "end": v(8.36, 1.17) * mm});
            skLineSegment(sketch, "E161.6", {"start": v(8.36, 1.17) * mm, "end": v(19.02, -4.98) * mm});
            skLineSegment(sketch, "E161.7", {"start": v(19.02, -4.98) * mm, "end": v(19.02, 16.98) * mm});
            skLineSegment(sketch, "E162.0", {"start": v(-8.68, 2.37) * mm, "end": v(-17.82, -2.9) * mm});
            skLineSegment(sketch, "E162.1", {"start": v(-8.68, 2.37) * mm, "end": v(8.68, 2.37) * mm});
            skLineSegment(sketch, "E162.2", {"start": v(-17.82, -2.9) * mm, "end": v(-17.82, 14.9) * mm});
            skLineSegment(sketch, "E162.3", {"start": v(8.68, 2.37) * mm, "end": v(17.82, -2.9) * mm});
            skLineSegment(sketch, "E162.4", {"start": v(-17.82, 14.9) * mm, "end": v(-8.68, 9.63) * mm});
            skLineSegment(sketch, "E162.5", {"start": v(8.68, 9.63) * mm, "end": v(-8.68, 9.63) * mm});
            skLineSegment(sketch, "E162.6", {"start": v(17.82, 14.9) * mm, "end": v(8.68, 9.63) * mm});
            skLineSegment(sketch, "E162.7", {"start": v(17.82, 14.9) * mm, "end": v(17.82, -2.9) * mm});
            skLineSegment(sketch, "E163.0", {"start": v(-17.42, 16.98) * mm, "end": v(-8.15, 11.63) * mm});
            skLineSegment(sketch, "E163.1", {"start": v(0, 27.04) * mm, "end": v(-17.42, 16.98) * mm});
            skLineSegment(sketch, "E163.2", {"start": v(-8.15, 11.63) * mm, "end": v(8.15, 11.63) * mm});
            skLineSegment(sketch, "E163.3", {"start": v(8.15, 11.63) * mm, "end": v(17.42, 16.98) * mm});
            skLineSegment(sketch, "E163.4", {"start": v(17.42, 16.98) * mm, "end": v(0, 27.04) * mm});
            skLineSegment(sketch, "E164.0", {"start": v(-8.15, 0.37) * mm, "end": v(-17.42, -4.98) * mm});
            skLineSegment(sketch, "E164.1", {"start": v(8.15, 0.37) * mm, "end": v(-8.15, 0.37) * mm});
            skLineSegment(sketch, "E164.2", {"start": v(-17.42, -4.98) * mm, "end": v(0, -15.04) * mm});
            skLineSegment(sketch, "E164.3", {"start": v(0, -15.04) * mm, "end": v(17.42, -4.98) * mm});
            skLineSegment(sketch, "E164.4", {"start": v(17.42, -4.98) * mm, "end": v(8.15, 0.37) * mm});
            skSolve(sketch);
        }
        {
            var Q0;
            Q0 = qSketchRegion(id + "F16", true);
            extrude(context, id + "F17", {"entities" : qUnion([Q0]), "operationType" : NewBodyOperationType.REMOVE, "oppositeDirection" : true, "depth" : 3 * mm, "offsetDistance" : 25 * mm});
        }
        {
            var Q0;
            Q0=makeQuery(id+"F17.boolean.opBoolean","SPLIT",FACE,{"disambiguationData":[TD([makeQuery(id+"F17.opExtrude","SWEPT_FACE",FACE,{"disambiguationData":[OSD([sQuery(id+"F16.wireOp",EDGE,"E162.0")])]})])],"derivedFrom":makeQuery(id+"F1.opExtrude","CAP_FACE",FACE,{"disambiguationData":[OSD([sQuery(id+"F0.wireOp",EDGE,"E0.bottom"),sQuery(id+"F0.wireOp",EDGE,"E0.top"),sQuery(id+"F0.wireOp",EDGE,"E0.left"),sQuery(id+"F0.wireOp",EDGE,"E0.right")])],"isStart":true})});
            var sketch = newSketch(context, id + "F18", { "sketchPlane" : qUnion([Q0])});
            skLineSegment(sketch, "E165.0", {"start": v(-2, 10.83) * mm, "end": v(2, 10.83) * mm});
            skLineSegment(sketch, "E165.1", {"start": v(14.38, 14.3) * mm, "end": v(10.92, 12.3) * mm});
            skLineSegment(sketch, "E165.2", {"start": v(-10.92, 12.3) * mm, "end": v(-14.38, 14.3) * mm});
            skLineSegment(sketch, "E165.3", {"start": v(19.02, 4) * mm, "end": v(19.02, 8) * mm});
            skLineSegment(sketch, "E165.4", {"start": v(-19.02, 4) * mm, "end": v(-19.02, 8) * mm});
            skLineSegment(sketch, "E165.5", {"start": v(-14.38, -2.3) * mm, "end": v(-10.92, -0.3) * mm});
            skLineSegment(sketch, "E165.6", {"start": v(2, 1.17) * mm, "end": v(-2, 1.17) * mm});
            skLineSegment(sketch, "E165.7", {"start": v(14.38, -2.3) * mm, "end": v(10.92, -0.3) * mm});
            skLineSegment(sketch, "E166.0", {"start": v(-2, 2.37) * mm, "end": v(2, 2.37) * mm});
            skLineSegment(sketch, "E166.1", {"start": v(-14.98, -1.26) * mm, "end": v(-11.52, 0.74) * mm});
            skLineSegment(sketch, "E166.2", {"start": v(11.52, 0.74) * mm, "end": v(14.98, -1.26) * mm});
            skLineSegment(sketch, "E166.3", {"start": v(-17.82, 8) * mm, "end": v(-17.82, 4) * mm});
            skLineSegment(sketch, "E166.4", {"start": v(17.82, 4) * mm, "end": v(17.82, 8) * mm});
            skLineSegment(sketch, "E166.5", {"start": v(14.98, 13.26) * mm, "end": v(11.52, 11.26) * mm});
            skLineSegment(sketch, "E166.6", {"start": v(2, 9.63) * mm, "end": v(-2, 9.63) * mm});
            skLineSegment(sketch, "E166.7", {"start": v(-11.52, 11.26) * mm, "end": v(-14.98, 13.26) * mm});
            skLineSegment(sketch, "E167", {"start": v(-17.82, 6) * mm, "end": v(-19.02, 6) * mm, "construction": true});
            skLineSegment(sketch, "E168", {"start": v(-17.82, 8) * mm, "end": v(-19.02, 8) * mm});
            skLineSegment(sketch, "E169", {"start": v(-17.82, 4) * mm, "end": v(-19.02, 4) * mm});
            skLineSegment(sketch, "E170", {"start": v(17.82, 6) * mm, "end": v(19.02, 6) * mm, "construction": true});
            skLineSegment(sketch, "E171", {"start": v(17.82, 8) * mm, "end": v(19.02, 8) * mm});
            skLineSegment(sketch, "E172", {"start": v(17.82, 4) * mm, "end": v(19.02, 4) * mm});
            skLineSegment(sketch, "E173", {"start": v(0, 9.63) * mm, "end": v(0, 10.83) * mm, "construction": true});
            skLineSegment(sketch, "E174", {"start": v(-13.25, -0.26) * mm, "end": v(-12.65, -1.3) * mm, "construction": true});
            skLineSegment(sketch, "E175", {"start": v(-13.25, 12.26) * mm, "end": v(-12.65, 13.3) * mm, "construction": true});
            skLineSegment(sketch, "E176", {"start": v(13.25, 12.26) * mm, "end": v(12.65, 13.3) * mm, "construction": true});
            skLineSegment(sketch, "E177", {"start": v(13.25, -0.26) * mm, "end": v(12.65, -1.3) * mm, "construction": true});
            skLineSegment(sketch, "E178", {"start": v(2, 1.17) * mm, "end": v(2, 2.37) * mm});
            skLineSegment(sketch, "E179", {"start": v(11.52, 0.74) * mm, "end": v(10.92, -0.3) * mm});
            skLineSegment(sketch, "E180", {"start": v(14.98, -1.26) * mm, "end": v(14.38, -2.3) * mm});
            skLineSegment(sketch, "E181", {"start": v(11.52, 11.26) * mm, "end": v(10.92, 12.3) * mm});
            skLineSegment(sketch, "E182", {"start": v(14.98, 13.26) * mm, "end": v(14.38, 14.3) * mm});
            skLineSegment(sketch, "E183", {"start": v(2, 9.63) * mm, "end": v(2, 10.83) * mm});
            skLineSegment(sketch, "E184", {"start": v(-2, 9.63) * mm, "end": v(-2, 10.83) * mm});
            skLineSegment(sketch, "E185", {"start": v(-11.52, 11.26) * mm, "end": v(-10.92, 12.3) * mm});
            skLineSegment(sketch, "E186", {"start": v(-14.98, 13.26) * mm, "end": v(-14.38, 14.3) * mm});
            skLineSegment(sketch, "E187", {"start": v(-11.52, 0.74) * mm, "end": v(-10.92, -0.3) * mm});
            skLineSegment(sketch, "E188", {"start": v(-14.98, -1.26) * mm, "end": v(-14.38, -2.3) * mm});
            skLineSegment(sketch, "E189", {"start": v(-2, 2.37) * mm, "end": v(-2, 1.17) * mm});
            skLineSegment(sketch, "E190", {"start": v(0, 2.37) * mm, "end": v(0, 1.17) * mm, "construction": true});
            skSolve(sketch);
        }
        {
            var Q0;
            Q0 = qSketchRegion(id + "F18", true);
            extrude(context, id + "F19", {"entities" : qUnion([Q0]), "oppositeDirection" : true, "depth" : 2 * mm, "offsetDistance" : 25 * mm});
        }
        {
            var Q0;
            Q0=makeQuery(id+"F17.boolean.opBoolean","SPLIT",BODY,{"disambiguationData":[OD(0.0)],"derivedFrom":makeQuery(id+"F1.opExtrude","SWEPT_BODY",BODY,{"disambiguationData":[OSD([sQuery(id+"F0.wireOp",EDGE,"E0.bottom"),sQuery(id+"F0.wireOp",EDGE,"E0.top"),sQuery(id+"F0.wireOp",EDGE,"E0.left"),sQuery(id+"F0.wireOp",EDGE,"E0.right")])]})});
            var Q1;
            Q1=makeQuery(id+"F17.boolean.opBoolean","SPLIT",BODY,{"disambiguationData":[OD(1.0)],"derivedFrom":makeQuery(id+"F1.opExtrude","SWEPT_BODY",BODY,{"disambiguationData":[OSD([sQuery(id+"F0.wireOp",EDGE,"E0.bottom"),sQuery(id+"F0.wireOp",EDGE,"E0.top"),sQuery(id+"F0.wireOp",EDGE,"E0.left"),sQuery(id+"F0.wireOp",EDGE,"E0.right")])]})});
            var Q2;
            Q2=makeQuery(id+"F19.opExtrude","SWEPT_BODY",BODY,{"disambiguationData":[OSD([sQuery(id+"F18.wireOp",EDGE,"E165.0"),sQuery(id+"F18.wireOp",EDGE,"E166.6"),sQuery(id+"F18.wireOp",EDGE,"E183"),sQuery(id+"F18.wireOp",EDGE,"E184")])]});
            var Q3;
            Q3=makeQuery(id+"F19.opExtrude","SWEPT_BODY",BODY,{"disambiguationData":[OSD([sQuery(id+"F18.wireOp",EDGE,"E165.1"),sQuery(id+"F18.wireOp",EDGE,"E166.5"),sQuery(id+"F18.wireOp",EDGE,"E181"),sQuery(id+"F18.wireOp",EDGE,"E182")])]});
            var Q4;
            Q4=makeQuery(id+"F19.opExtrude","SWEPT_BODY",BODY,{"disambiguationData":[OSD([sQuery(id+"F18.wireOp",EDGE,"E165.2"),sQuery(id+"F18.wireOp",EDGE,"E166.7"),sQuery(id+"F18.wireOp",EDGE,"E185"),sQuery(id+"F18.wireOp",EDGE,"E186")])]});
            var Q5;
            Q5=makeQuery(id+"F19.opExtrude","SWEPT_BODY",BODY,{"disambiguationData":[OSD([sQuery(id+"F18.wireOp",EDGE,"E165.3"),sQuery(id+"F18.wireOp",EDGE,"E166.4"),sQuery(id+"F18.wireOp",EDGE,"E171"),sQuery(id+"F18.wireOp",EDGE,"E172")])]});
            var Q6;
            Q6=makeQuery(id+"F19.opExtrude","SWEPT_BODY",BODY,{"disambiguationData":[OSD([sQuery(id+"F18.wireOp",EDGE,"E165.4"),sQuery(id+"F18.wireOp",EDGE,"E166.3"),sQuery(id+"F18.wireOp",EDGE,"E168"),sQuery(id+"F18.wireOp",EDGE,"E169")])]});
            var Q7;
            Q7=makeQuery(id+"F19.opExtrude","SWEPT_BODY",BODY,{"disambiguationData":[OSD([sQuery(id+"F18.wireOp",EDGE,"E165.5"),sQuery(id+"F18.wireOp",EDGE,"E166.1"),sQuery(id+"F18.wireOp",EDGE,"E187"),sQuery(id+"F18.wireOp",EDGE,"E188")])]});
            var Q8;
            Q8=makeQuery(id+"F19.opExtrude","SWEPT_BODY",BODY,{"disambiguationData":[OSD([sQuery(id+"F18.wireOp",EDGE,"E165.6"),sQuery(id+"F18.wireOp",EDGE,"E166.0"),sQuery(id+"F18.wireOp",EDGE,"E178"),sQuery(id+"F18.wireOp",EDGE,"E189")])]});
            var Q9;
            Q9=makeQuery(id+"F19.opExtrude","SWEPT_BODY",BODY,{"disambiguationData":[OSD([sQuery(id+"F18.wireOp",EDGE,"E165.7"),sQuery(id+"F18.wireOp",EDGE,"E166.2"),sQuery(id+"F18.wireOp",EDGE,"E179"),sQuery(id+"F18.wireOp",EDGE,"E180")])]});
            booleanBodies(context, id + "F20", {"operationType" : BooleanOperationType.UNION, "tools" : qUnion([Q0, Q1, Q2, Q3, Q4, Q5, Q6, Q7, Q8, Q9])});
        }
        {
            var Q0;
            {var subQ0=sQuery(id+"F0.wireOp",EDGE,"E0.top");var subQ1=sQuery(id+"F0.wireOp",EDGE,"E0.right");var subQ2=sQuery(id+"F0.wireOp",EDGE,"E0.bottom");var subQ3=sQuery(id+"F0.wireOp",EDGE,"E0.left");var subQ4=makeQuery(id+"F1.opExtrude","CAP_FACE",FACE,{"disambiguationData":[OSD([subQ2,subQ0,subQ3,subQ1])],"isStart":true});Q0=makeQuery(id+"F20.opBoolean","MERGE",FACE,{"derivedFrom":[makeQuery(id+"F17.boolean.opBoolean","SPLIT",FACE,{"disambiguationData":[TD([makeQuery(id+"F17.opExtrude","SWEPT_FACE",FACE,{"disambiguationData":[OSD([sQuery(id+"F16.wireOp",EDGE,"E162.0")])]})])],"derivedFrom":subQ4}),makeQuery(id+"F17.boolean.opBoolean","SPLIT",FACE,{"disambiguationData":[TD([makeQuery(id+"F1.opExtrude","SWEPT_FACE",FACE,{"disambiguationData":[OSD([subQ2])]})])],"derivedFrom":subQ4}),makeQuery(id+"F19.opExtrude","CAP_FACE",FACE,{"disambiguationData":[OSD([sQuery(id+"F18.wireOp",EDGE,"E165.0"),sQuery(id+"F18.wireOp",EDGE,"E166.6"),sQuery(id+"F18.wireOp",EDGE,"E183"),sQuery(id+"F18.wireOp",EDGE,"E184")])],"isStart":true}),makeQuery(id+"F19.opExtrude","CAP_FACE",FACE,{"disambiguationData":[OSD([sQuery(id+"F18.wireOp",EDGE,"E165.1"),sQuery(id+"F18.wireOp",EDGE,"E166.5"),sQuery(id+"F18.wireOp",EDGE,"E181"),sQuery(id+"F18.wireOp",EDGE,"E182")])],"isStart":true}),makeQuery(id+"F19.opExtrude","CAP_FACE",FACE,{"disambiguationData":[OSD([sQuery(id+"F18.wireOp",EDGE,"E165.2"),sQuery(id+"F18.wireOp",EDGE,"E166.7"),sQuery(id+"F18.wireOp",EDGE,"E185"),sQuery(id+"F18.wireOp",EDGE,"E186")])],"isStart":true}),makeQuery(id+"F19.opExtrude","CAP_FACE",FACE,{"disambiguationData":[OSD([sQuery(id+"F18.wireOp",EDGE,"E165.3"),sQuery(id+"F18.wireOp",EDGE,"E166.4"),sQuery(id+"F18.wireOp",EDGE,"E171"),sQuery(id+"F18.wireOp",EDGE,"E172")])],"isStart":true}),makeQuery(id+"F19.opExtrude","CAP_FACE",FACE,{"disambiguationData":[OSD([sQuery(id+"F18.wireOp",EDGE,"E165.4"),sQuery(id+"F18.wireOp",EDGE,"E166.3"),sQuery(id+"F18.wireOp",EDGE,"E168"),sQuery(id+"F18.wireOp",EDGE,"E169")])],"isStart":true}),makeQuery(id+"F19.opExtrude","CAP_FACE",FACE,{"disambiguationData":[OSD([sQuery(id+"F18.wireOp",EDGE,"E165.5"),sQuery(id+"F18.wireOp",EDGE,"E166.1"),sQuery(id+"F18.wireOp",EDGE,"E187"),sQuery(id+"F18.wireOp",EDGE,"E188")])],"isStart":true}),makeQuery(id+"F19.opExtrude","CAP_FACE",FACE,{"disambiguationData":[OSD([sQuery(id+"F18.wireOp",EDGE,"E165.6"),sQuery(id+"F18.wireOp",EDGE,"E166.0"),sQuery(id+"F18.wireOp",EDGE,"E178"),sQuery(id+"F18.wireOp",EDGE,"E189")])],"isStart":true}),makeQuery(id+"F19.opExtrude","CAP_FACE",FACE,{"disambiguationData":[OSD([sQuery(id+"F18.wireOp",EDGE,"E165.7"),sQuery(id+"F18.wireOp",EDGE,"E166.2"),sQuery(id+"F18.wireOp",EDGE,"E179"),sQuery(id+"F18.wireOp",EDGE,"E180")])],"isStart":true})]});}
            var sketch = newSketch(context, id + "F21", { "sketchPlane" : qUnion([Q0])});
            skLineSegment(sketch, "E191.0", {"start": v(70, 23.25) * mm, "end": v(63.24, 23.25) * mm});
            skLineSegment(sketch, "E191.1", {"start": v(59.25, 1.24) * mm, "end": v(59.25, 18.76) * mm});
            skLineSegment(sketch, "E191.2", {"start": v(70, -2.75) * mm, "end": v(63.24, -2.75) * mm});
            skLineSegment(sketch, "E192.0", {"start": v(70, -5.75) * mm, "end": v(60.24, -5.75) * mm});
            skLineSegment(sketch, "E192.1", {"start": v(56.25, -1.76) * mm, "end": v(56.25, 21.76) * mm});
            skLineSegment(sketch, "E192.2", {"start": v(70, 26.25) * mm, "end": v(60.24, 26.25) * mm});
            skLineSegment(sketch, "E193", {"start": v(70, 23.25) * mm, "end": v(70, 26.25) * mm});
            skLineSegment(sketch, "E194", {"start": v(70, -2.75) * mm, "end": v(70, -5.75) * mm});
            skLineSegment(sketch, "E195.0", {"start": v(59.25, 1.24) * mm, "end": v(56.25, -1.76) * mm});
            skLineSegment(sketch, "E196.0", {"start": v(63.24, -2.75) * mm, "end": v(60.24, -5.75) * mm});
            skLineSegment(sketch, "E197.0", {"start": v(63.24, 23.25) * mm, "end": v(60.24, 26.25) * mm});
            skLineSegment(sketch, "E198.0", {"start": v(59.25, 18.76) * mm, "end": v(56.25, 21.76) * mm});
            skLineSegment(sketch, "E199.0", {"start": v(53.25, -30) * mm, "end": v(53.25, -21.24) * mm});
            skLineSegment(sketch, "E199.1", {"start": v(-8.76, -17.25) * mm, "end": v(-4.17, -17.25) * mm});
            skLineSegment(sketch, "E199.2", {"start": v(-12.75, -30.25) * mm, "end": v(-12.75, -21.24) * mm});
            skLineSegment(sketch, "E200.0", {"start": v(56.25, -30) * mm, "end": v(56.25, -18.24) * mm});
            skLineSegment(sketch, "E200.1", {"start": v(-11.76, -14.25) * mm, "end": v(-9.37, -14.25) * mm});
            skLineSegment(sketch, "E200.2", {"start": v(-15.75, -30.25) * mm, "end": v(-15.75, -18.24) * mm});
            skLineSegment(sketch, "E201.0", {"start": v(-4.17, -17.25) * mm, "end": v(-9.37, -14.25) * mm});
            skLineSegment(sketch, "E201.1", {"start": v(9.37, -14.25) * mm, "end": v(4.17, -17.25) * mm});
            skLineSegment(sketch, "E202.0", {"start": v(53.25, -21.24) * mm, "end": v(56.25, -18.24) * mm});
            skLineSegment(sketch, "E203.0", {"start": v(48.76, -17.25) * mm, "end": v(51.76, -14.25) * mm});
            skLineSegment(sketch, "E204.0", {"start": v(-15.75, -18.24) * mm, "end": v(-12.75, -21.24) * mm});
            skLineSegment(sketch, "E205.0", {"start": v(-11.76, -14.25) * mm, "end": v(-8.76, -17.25) * mm});
            skLineSegment(sketch, "E206.trimOffspring", {"start": v(9.37, -14.25) * mm, "end": v(51.76, -14.25) * mm});
            skLineSegment(sketch, "E207.trimOffspring", {"start": v(4.17, -17.25) * mm, "end": v(48.76, -17.25) * mm});
            skLineSegment(sketch, "E208", {"start": v(-15.75, -30.25) * mm, "end": v(-12.75, -30.25) * mm});
            skLineSegment(sketch, "E209", {"start": v(53.25, -30) * mm, "end": v(56.25, -30) * mm});
            skLineSegment(sketch, "E210.0", {"start": v(-69.25, -27.25) * mm, "end": v(-69.25, -7.1) * mm});
            skLineSegment(sketch, "E211", {"start": v(-66, 0) * mm, "end": v(-69.25, 0) * mm, "construction": true});
            skLineSegment(sketch, "E212", {"start": v(-66.25, 4) * mm, "end": v(-69.25, 7) * mm});
            skLineSegment(sketch, "E213", {"start": v(-66.25, -4) * mm, "end": v(-69.25, -7.1) * mm});
            skLineSegment(sketch, "E214.trimOffspring", {"start": v(-69.25, 7) * mm, "end": v(-69.25, 26.25) * mm});
            skLineSegment(sketch, "E215.trimOffspring", {"start": v(-66.25, 4) * mm, "end": v(-66.25, 29.25) * mm});
            skLineSegment(sketch, "E216", {"start": v(-66.25, 29.25) * mm, "end": v(-69.25, 26.25) * mm});
            skPoint(sketch, "E217.orphan", {"position": v(-69.25, 32.21) * mm});
            skPoint(sketch, "E218.orphan", {"position": v(-66.25, 32) * mm});
            skLineSegment(sketch, "E219", {"start": v(-66.25, -30.25) * mm, "end": v(-66.25, -4) * mm});
            skLineSegment(sketch, "E220", {"start": v(-66.25, -30.25) * mm, "end": v(-69.25, -27.25) * mm});
            skPoint(sketch, "E221.orphan", {"position": v(-69.25, -32.21) * mm});
            skLineSegment(sketch, "E222", {"start": v(-57.25, -30.25) * mm, "end": v(-44, -30.25) * mm});
            skLineSegment(sketch, "E223", {"start": v(-19.75, -27.25) * mm, "end": v(-33, -27.25) * mm});
            skLineSegment(sketch, "E224", {"start": v(-60.25, -27.25) * mm, "end": v(-57.25, -30.25) * mm});
            skLineSegment(sketch, "E225", {"start": v(-19.75, -27.25) * mm, "end": v(-22.75, -30.25) * mm});
            skPoint(sketch, "E226.orphan", {"position": v(-15.75, -27.25) * mm});
            skPoint(sketch, "E227.orphan", {"position": v(-66.25, -27.25) * mm});
            skLineSegment(sketch, "E228", {"start": v(-40, -30.25) * mm, "end": v(-40, -27.25) * mm, "construction": true});
            skLineSegment(sketch, "E229", {"start": v(-44, -30.25) * mm, "end": v(-47, -27.25) * mm});
            skLineSegment(sketch, "E230", {"start": v(-36, -30.25) * mm, "end": v(-33, -27.25) * mm});
            skLineSegment(sketch, "E231.trimOffspring", {"start": v(-36, -30.25) * mm, "end": v(-22.75, -30.25) * mm});
            skLineSegment(sketch, "E232.trimOffspring", {"start": v(-47, -27.25) * mm, "end": v(-60.25, -27.25) * mm});
            skLineSegment(sketch, "E233", {"start": v(-57.25, 29.25) * mm, "end": v(-41.8, 29.25) * mm});
            skLineSegment(sketch, "E234.0", {"start": v(-9.37, 26.25) * mm, "end": v(-4.17, 29.25) * mm});
            skLineSegment(sketch, "E235", {"start": v(-60.25, 26.25) * mm, "end": v(-38.8, 26.25) * mm});
            skLineSegment(sketch, "E236", {"start": v(-60.25, 26.25) * mm, "end": v(-57.25, 29.25) * mm});
            skPoint(sketch, "E237.orphan", {"position": v(-66.25, 26.25) * mm});
            skLineSegment(sketch, "E238", {"start": v(9.37, 26.25) * mm, "end": v(27.8, 26.25) * mm});
            skLineSegment(sketch, "E239", {"start": v(4.17, 29.25) * mm, "end": v(24.8, 29.25) * mm});
            skLineSegment(sketch, "E240", {"start": v(54.24, 26.25) * mm, "end": v(51.24, 29.25) * mm});
            skPoint(sketch, "E241.start.orphan", {"position": v(70, 29.25) * mm});
            skLineSegment(sketch, "E242.0", {"start": v(4.17, 29.25) * mm, "end": v(9.37, 26.25) * mm});
            skLineSegment(sketch, "E243", {"start": v(31.8, 26.25) * mm, "end": v(31.8, 29.25) * mm, "construction": true});
            skLineSegment(sketch, "E244", {"start": v(27.8, 26.25) * mm, "end": v(24.8, 29.25) * mm});
            skLineSegment(sketch, "E245", {"start": v(35.8, 26.25) * mm, "end": v(38.8, 29.25) * mm});
            skLineSegment(sketch, "E246", {"start": v(-34.8, 26.25) * mm, "end": v(-34.8, 29.25) * mm, "construction": true});
            skLineSegment(sketch, "E247", {"start": v(-38.8, 26.25) * mm, "end": v(-41.8, 29.25) * mm});
            skLineSegment(sketch, "E248", {"start": v(-30.8, 26.25) * mm, "end": v(-27.8, 29.25) * mm});
            skLineSegment(sketch, "E249.trimOffspring", {"start": v(38.8, 29.25) * mm, "end": v(51.24, 29.25) * mm});
            skLineSegment(sketch, "E250.trimOffspring", {"start": v(35.8, 26.25) * mm, "end": v(54.24, 26.25) * mm});
            skLineSegment(sketch, "E251.trimOffspring", {"start": v(-30.8, 26.25) * mm, "end": v(-9.37, 26.25) * mm});
            skLineSegment(sketch, "E252.trimOffspring", {"start": v(-27.8, 29.25) * mm, "end": v(-4.17, 29.25) * mm});
            skLineSegment(sketch, "E253.bottom", {"start": v(-57.25, 20.25) * mm, "end": v(-28.02, 20.25) * mm});
            skLineSegment(sketch, "E253.left", {"start": v(-60.25, 17.25) * mm, "end": v(-60.25, -18.25) * mm});
            skLineSegment(sketch, "E253.right", {"start": v(-25.02, 17.25) * mm, "end": v(-25.02, -18.25) * mm});
            skLineSegment(sketch, "E254", {"start": v(-57.25, -21.25) * mm, "end": v(-28.02, -21.25) * mm});
            skLineSegment(sketch, "E255", {"start": v(-19.02, 16.98) * mm, "end": v(-19.02, 26.25) * mm, "construction": true});
            skLineSegment(sketch, "E256.0", {"start": v(-54.25, 17.25) * mm, "end": v(-31.02, 17.25) * mm});
            skLineSegment(sketch, "E256.1", {"start": v(-57.25, 14.25) * mm, "end": v(-57.25, -15.25) * mm});
            skLineSegment(sketch, "E256.2", {"start": v(-54.25, -18.25) * mm, "end": v(-31.02, -18.25) * mm});
            skLineSegment(sketch, "E256.3", {"start": v(-28.02, 14.25) * mm, "end": v(-28.02, -15.25) * mm});
            skLineSegment(sketch, "E257", {"start": v(-57.25, 20.25) * mm, "end": v(-54.25, 17.25) * mm});
            skLineSegment(sketch, "E258", {"start": v(-60.25, 17.25) * mm, "end": v(-57.25, 14.25) * mm});
            skLineSegment(sketch, "E259", {"start": v(-28.02, 20.25) * mm, "end": v(-31.02, 17.25) * mm});
            skLineSegment(sketch, "E260", {"start": v(-25.02, 17.25) * mm, "end": v(-28.02, 14.25) * mm});
            skLineSegment(sketch, "E261", {"start": v(-60.25, -18.25) * mm, "end": v(-57.25, -15.25) * mm});
            skLineSegment(sketch, "E262", {"start": v(-57.25, -21.25) * mm, "end": v(-54.25, -18.25) * mm});
            skLineSegment(sketch, "E263", {"start": v(-25.02, -18.25) * mm, "end": v(-28.02, -15.25) * mm});
            skLineSegment(sketch, "E264", {"start": v(-28.02, -21.25) * mm, "end": v(-31.02, -18.25) * mm});
            skLineSegment(sketch, "E265.0", {"start": v(-51.25, -15.25) * mm, "end": v(-34.02, -15.25) * mm});
            skLineSegment(sketch, "E265.1", {"start": v(-54.25, 11.25) * mm, "end": v(-54.25, -12.25) * mm});
            skLineSegment(sketch, "E265.2", {"start": v(-51.25, 14.25) * mm, "end": v(-34.02, 14.25) * mm});
            skLineSegment(sketch, "E265.3", {"start": v(-31.02, 11.25) * mm, "end": v(-31.02, -12.25) * mm});
            skLineSegment(sketch, "E266.0", {"start": v(-48.25, -12.25) * mm, "end": v(-37.02, -12.25) * mm});
            skLineSegment(sketch, "E266.1", {"start": v(-51.25, 8.25) * mm, "end": v(-51.25, -9.25) * mm});
            skLineSegment(sketch, "E266.2", {"start": v(-48.25, 11.25) * mm, "end": v(-37.02, 11.25) * mm});
            skLineSegment(sketch, "E266.3", {"start": v(-34.02, 8.25) * mm, "end": v(-34.02, -9.25) * mm});
            skLineSegment(sketch, "E267.0", {"start": v(-45.25, -9.25) * mm, "end": v(-40.02, -9.25) * mm});
            skLineSegment(sketch, "E267.1", {"start": v(-48.25, 5.25) * mm, "end": v(-48.25, 0.02) * mm});
            skLineSegment(sketch, "E267.2", {"start": v(-45.25, 8.25) * mm, "end": v(-40.02, 8.25) * mm});
            skLineSegment(sketch, "E267.3", {"start": v(-37.02, 5.25) * mm, "end": v(-37.02, 0.02) * mm});
            skPoint(sketch, "E268.orphan", {"position": v(-60.25, -21.25) * mm});
            skLineSegment(sketch, "E269.trimOffspring", {"start": v(-51.25, -15.25) * mm, "end": v(-48.25, -12.25) * mm});
            skLineSegment(sketch, "E270.trimOffspring", {"start": v(-54.25, -12.25) * mm, "end": v(-51.25, -9.25) * mm});
            skLineSegment(sketch, "E271.trimOffspring", {"start": v(-45.25, -9.25) * mm, "end": v(-42.63, -6.63) * mm});
            skLineSegment(sketch, "E272.trimOffspring", {"start": v(-34.02, -15.25) * mm, "end": v(-37.02, -12.25) * mm});
            skPoint(sketch, "E273.orphan", {"position": v(-25.02, -21.25) * mm});
            skLineSegment(sketch, "E274.trimOffspring", {"start": v(-31.02, -12.25) * mm, "end": v(-34.02, -9.25) * mm});
            skLineSegment(sketch, "E275.trimOffspring", {"start": v(-40.02, -9.25) * mm, "end": v(-42.63, -6.63) * mm});
            skLineSegment(sketch, "E276.trimOffspring", {"start": v(-31.02, 11.25) * mm, "end": v(-34.02, 8.25) * mm});
            skPoint(sketch, "E277.orphan", {"position": v(-25.02, 20.25) * mm});
            skLineSegment(sketch, "E278.trimOffspring", {"start": v(-34.02, 14.25) * mm, "end": v(-37.02, 11.25) * mm});
            skPoint(sketch, "E279.orphan", {"position": v(-60.25, 20.25) * mm});
            skLineSegment(sketch, "E280.trimOffspring", {"start": v(-51.25, 14.25) * mm, "end": v(-48.25, 11.25) * mm});
            skLineSegment(sketch, "E281.trimOffspring", {"start": v(-54.25, 11.25) * mm, "end": v(-51.25, 8.25) * mm});
            skLineSegment(sketch, "E282.trimOffspring", {"start": v(-48.25, 5.25) * mm, "end": v(-45.63, 2.63) * mm});
            skLineSegment(sketch, "E283.trimOffspring", {"start": v(-45.25, 8.25) * mm, "end": v(-42.63, 5.63) * mm});
            skLineSegment(sketch, "E284.trimOffspring", {"start": v(-40.02, 8.25) * mm, "end": v(-42.63, 5.63) * mm});
            skLineSegment(sketch, "E285.trimOffspring", {"start": v(-37.02, 5.25) * mm, "end": v(-39.63, 2.63) * mm});
            skLineSegment(sketch, "E286.trimOffspring", {"start": v(-45.5, -3.76) * mm, "end": v(-48.25, -1.02) * mm});
            skLineSegment(sketch, "E287.trimOffspring", {"start": v(-39.38, -3.38) * mm, "end": v(-37.02, -1.02) * mm});
            skLineSegment(sketch, "E288.trimOffspring", {"start": v(-37.02, -1.02) * mm, "end": v(-37.02, -5.75) * mm});
            skLineSegment(sketch, "E289", {"start": v(-37.02, -5.75) * mm, "end": v(-39.38, -3.38) * mm});
            skLineSegment(sketch, "E290.trimOffspring", {"start": v(-48.25, -1.02) * mm, "end": v(-48.25, -6.5) * mm});
            skLineSegment(sketch, "E291.trimOffspring", {"start": v(-45.63, 2.63) * mm, "end": v(-48.25, 0.02) * mm});
            skLineSegment(sketch, "E292.trimOffspring", {"start": v(-39.63, 2.63) * mm, "end": v(-37.02, 0.02) * mm});
            skLineSegment(sketch, "E293", {"start": v(-48.25, -6.5) * mm, "end": v(-45.5, -3.76) * mm});
            skSolve(sketch);
        }
        {
            var Q0;
            Q0 = qSketchRegion(id + "F21", true);
            extrude(context, id + "F22", {"entities" : qUnion([Q0]), "operationType" : NewBodyOperationType.REMOVE, "oppositeDirection" : true, "depth" : 25 * mm, "offsetDistance" : 25 * mm});
        }
        {
            var Q0;
            {var subQ0=sQuery(id+"F0.wireOp",EDGE,"E0.top");var subQ1=sQuery(id+"F0.wireOp",EDGE,"E0.right");var subQ2=sQuery(id+"F0.wireOp",EDGE,"E0.bottom");var subQ3=sQuery(id+"F0.wireOp",EDGE,"E0.left");var subQ4=makeQuery(id+"F1.opExtrude","CAP_FACE",FACE,{"disambiguationData":[OSD([subQ2,subQ0,subQ3,subQ1])],"isStart":true});Q0=makeQuery(id+"F20.opBoolean","MERGE",FACE,{"derivedFrom":[makeQuery(id+"F17.boolean.opBoolean","SPLIT",FACE,{"disambiguationData":[TD([makeQuery(id+"F17.opExtrude","SWEPT_FACE",FACE,{"disambiguationData":[OSD([sQuery(id+"F16.wireOp",EDGE,"E162.0")])]})])],"derivedFrom":subQ4}),makeQuery(id+"F17.boolean.opBoolean","SPLIT",FACE,{"disambiguationData":[TD([makeQuery(id+"F1.opExtrude","SWEPT_FACE",FACE,{"disambiguationData":[OSD([subQ2])]})])],"derivedFrom":subQ4}),makeQuery(id+"F19.opExtrude","CAP_FACE",FACE,{"disambiguationData":[OSD([sQuery(id+"F18.wireOp",EDGE,"E165.0"),sQuery(id+"F18.wireOp",EDGE,"E166.6"),sQuery(id+"F18.wireOp",EDGE,"E183"),sQuery(id+"F18.wireOp",EDGE,"E184")])],"isStart":true}),makeQuery(id+"F19.opExtrude","CAP_FACE",FACE,{"disambiguationData":[OSD([sQuery(id+"F18.wireOp",EDGE,"E165.1"),sQuery(id+"F18.wireOp",EDGE,"E166.5"),sQuery(id+"F18.wireOp",EDGE,"E181"),sQuery(id+"F18.wireOp",EDGE,"E182")])],"isStart":true}),makeQuery(id+"F19.opExtrude","CAP_FACE",FACE,{"disambiguationData":[OSD([sQuery(id+"F18.wireOp",EDGE,"E165.2"),sQuery(id+"F18.wireOp",EDGE,"E166.7"),sQuery(id+"F18.wireOp",EDGE,"E185"),sQuery(id+"F18.wireOp",EDGE,"E186")])],"isStart":true}),makeQuery(id+"F19.opExtrude","CAP_FACE",FACE,{"disambiguationData":[OSD([sQuery(id+"F18.wireOp",EDGE,"E165.3"),sQuery(id+"F18.wireOp",EDGE,"E166.4"),sQuery(id+"F18.wireOp",EDGE,"E171"),sQuery(id+"F18.wireOp",EDGE,"E172")])],"isStart":true}),makeQuery(id+"F19.opExtrude","CAP_FACE",FACE,{"disambiguationData":[OSD([sQuery(id+"F18.wireOp",EDGE,"E165.4"),sQuery(id+"F18.wireOp",EDGE,"E166.3"),sQuery(id+"F18.wireOp",EDGE,"E168"),sQuery(id+"F18.wireOp",EDGE,"E169")])],"isStart":true}),makeQuery(id+"F19.opExtrude","CAP_FACE",FACE,{"disambiguationData":[OSD([sQuery(id+"F18.wireOp",EDGE,"E165.5"),sQuery(id+"F18.wireOp",EDGE,"E166.1"),sQuery(id+"F18.wireOp",EDGE,"E187"),sQuery(id+"F18.wireOp",EDGE,"E188")])],"isStart":true}),makeQuery(id+"F19.opExtrude","CAP_FACE",FACE,{"disambiguationData":[OSD([sQuery(id+"F18.wireOp",EDGE,"E165.6"),sQuery(id+"F18.wireOp",EDGE,"E166.0"),sQuery(id+"F18.wireOp",EDGE,"E178"),sQuery(id+"F18.wireOp",EDGE,"E189")])],"isStart":true}),makeQuery(id+"F19.opExtrude","CAP_FACE",FACE,{"disambiguationData":[OSD([sQuery(id+"F18.wireOp",EDGE,"E165.7"),sQuery(id+"F18.wireOp",EDGE,"E166.2"),sQuery(id+"F18.wireOp",EDGE,"E179"),sQuery(id+"F18.wireOp",EDGE,"E180")])],"isStart":true})]});}
            var sketch = newSketch(context, id + "F23", { "sketchPlane" : qUnion([Q0])});
            skLineSegment(sketch, "E294", {"start": v(-69.25, -7.1) * mm, "end": v(-69.25, 16.62) * mm});
            skLineSegment(sketch, "E295", {"start": v(-69.25, 16.62) * mm, "end": v(-63.25, 16.62) * mm});
            skPoint(sketch, "E295.endSnap0", {"position": v(-66.25, 16.62) * mm});
            skLineSegment(sketch, "E296", {"start": v(-63.25, 16.62) * mm, "end": v(-63.25, -7.1) * mm});
            skLineSegment(sketch, "E297", {"start": v(-69.25, -7.1) * mm, "end": v(-63.25, -7.1) * mm});
            skSolve(sketch);
        }
        {
            var Q0;
            Q0 = qSketchRegion(id + "F23", true);
            extrude(context, id + "F24", {"entities" : qUnion([Q0]), "operationType" : NewBodyOperationType.REMOVE, "oppositeDirection" : true, "depth" : 25 * mm, "offsetDistance" : 25 * mm});
        }
        {
            var Q0;
            {var subQ0=sQuery(id+"F0.wireOp",EDGE,"E0.top");var subQ1=sQuery(id+"F0.wireOp",EDGE,"E0.right");var subQ2=sQuery(id+"F0.wireOp",EDGE,"E0.bottom");var subQ3=sQuery(id+"F0.wireOp",EDGE,"E0.left");var subQ4=makeQuery(id+"F1.opExtrude","CAP_FACE",FACE,{"disambiguationData":[OSD([subQ2,subQ0,subQ3,subQ1])],"isStart":true});Q0=makeQuery(id+"F20.opBoolean","MERGE",FACE,{"derivedFrom":[makeQuery(id+"F17.boolean.opBoolean","SPLIT",FACE,{"disambiguationData":[TD([makeQuery(id+"F17.opExtrude","SWEPT_FACE",FACE,{"disambiguationData":[OSD([sQuery(id+"F16.wireOp",EDGE,"E162.0")])]})])],"derivedFrom":subQ4}),makeQuery(id+"F17.boolean.opBoolean","SPLIT",FACE,{"disambiguationData":[TD([makeQuery(id+"F1.opExtrude","SWEPT_FACE",FACE,{"disambiguationData":[OSD([subQ2])]})])],"derivedFrom":subQ4}),makeQuery(id+"F19.opExtrude","CAP_FACE",FACE,{"disambiguationData":[OSD([sQuery(id+"F18.wireOp",EDGE,"E165.0"),sQuery(id+"F18.wireOp",EDGE,"E166.6"),sQuery(id+"F18.wireOp",EDGE,"E183"),sQuery(id+"F18.wireOp",EDGE,"E184")])],"isStart":true}),makeQuery(id+"F19.opExtrude","CAP_FACE",FACE,{"disambiguationData":[OSD([sQuery(id+"F18.wireOp",EDGE,"E165.1"),sQuery(id+"F18.wireOp",EDGE,"E166.5"),sQuery(id+"F18.wireOp",EDGE,"E181"),sQuery(id+"F18.wireOp",EDGE,"E182")])],"isStart":true}),makeQuery(id+"F19.opExtrude","CAP_FACE",FACE,{"disambiguationData":[OSD([sQuery(id+"F18.wireOp",EDGE,"E165.2"),sQuery(id+"F18.wireOp",EDGE,"E166.7"),sQuery(id+"F18.wireOp",EDGE,"E185"),sQuery(id+"F18.wireOp",EDGE,"E186")])],"isStart":true}),makeQuery(id+"F19.opExtrude","CAP_FACE",FACE,{"disambiguationData":[OSD([sQuery(id+"F18.wireOp",EDGE,"E165.3"),sQuery(id+"F18.wireOp",EDGE,"E166.4"),sQuery(id+"F18.wireOp",EDGE,"E171"),sQuery(id+"F18.wireOp",EDGE,"E172")])],"isStart":true}),makeQuery(id+"F19.opExtrude","CAP_FACE",FACE,{"disambiguationData":[OSD([sQuery(id+"F18.wireOp",EDGE,"E165.4"),sQuery(id+"F18.wireOp",EDGE,"E166.3"),sQuery(id+"F18.wireOp",EDGE,"E168"),sQuery(id+"F18.wireOp",EDGE,"E169")])],"isStart":true}),makeQuery(id+"F19.opExtrude","CAP_FACE",FACE,{"disambiguationData":[OSD([sQuery(id+"F18.wireOp",EDGE,"E165.5"),sQuery(id+"F18.wireOp",EDGE,"E166.1"),sQuery(id+"F18.wireOp",EDGE,"E187"),sQuery(id+"F18.wireOp",EDGE,"E188")])],"isStart":true}),makeQuery(id+"F19.opExtrude","CAP_FACE",FACE,{"disambiguationData":[OSD([sQuery(id+"F18.wireOp",EDGE,"E165.6"),sQuery(id+"F18.wireOp",EDGE,"E166.0"),sQuery(id+"F18.wireOp",EDGE,"E178"),sQuery(id+"F18.wireOp",EDGE,"E189")])],"isStart":true}),makeQuery(id+"F19.opExtrude","CAP_FACE",FACE,{"disambiguationData":[OSD([sQuery(id+"F18.wireOp",EDGE,"E165.7"),sQuery(id+"F18.wireOp",EDGE,"E166.2"),sQuery(id+"F18.wireOp",EDGE,"E179"),sQuery(id+"F18.wireOp",EDGE,"E180")])],"isStart":true})]});}
            var sketch = newSketch(context, id + "F25", { "sketchPlane" : qUnion([Q0])});
            skLineSegment(sketch, "E298", {"start": v(-69.25, -27.25) * mm, "end": v(-69.25, -7.1) * mm});
            skLineSegment(sketch, "E299", {"start": v(-66.25, -7.1) * mm, "end": v(-69.25, -7.1) * mm});
            skLineSegment(sketch, "E300", {"start": v(-66.25, -7.1) * mm, "end": v(-66.25, -30.25) * mm});
            skLineSegment(sketch, "E301", {"start": v(-66.25, 16.62) * mm, "end": v(-69.25, 16.62) * mm});
            skLineSegment(sketch, "E302", {"start": v(-69.25, 16.62) * mm, "end": v(-69.25, 26.25) * mm});
            skLineSegment(sketch, "E303", {"start": v(-66.25, 16.62) * mm, "end": v(-66.25, 29.25) * mm});
            skLineSegment(sketch, "E304", {"start": v(-69.25, -27.25) * mm, "end": v(-66.25, -30.25) * mm});
            skLineSegment(sketch, "E305", {"start": v(-69.25, 26.25) * mm, "end": v(-66.25, 29.25) * mm});
            skLineSegment(sketch, "E306", {"start": v(-39.38, -3.38) * mm, "end": v(-37.02, -5.75) * mm});
            skLineSegment(sketch, "E307", {"start": v(-37.02, -5.75) * mm, "end": v(-37.02, -1.02) * mm});
            skLineSegment(sketch, "E308", {"start": v(-37.02, -1.02) * mm, "end": v(-39.38, -3.38) * mm});
            skLineSegment(sketch, "E309", {"start": v(-40.02, -9.25) * mm, "end": v(-42.63, -6.63) * mm});
            skLineSegment(sketch, "E310", {"start": v(-42.63, -6.63) * mm, "end": v(-45.25, -9.25) * mm});
            skLineSegment(sketch, "E311", {"start": v(-45.25, -9.25) * mm, "end": v(-40.02, -9.25) * mm});
            skLineSegment(sketch, "E312", {"start": v(-48.25, -6.5) * mm, "end": v(-45.5, -3.76) * mm});
            skLineSegment(sketch, "E313", {"start": v(-45.5, -3.76) * mm, "end": v(-48.25, -1.02) * mm});
            skLineSegment(sketch, "E314", {"start": v(-48.25, -1.02) * mm, "end": v(-48.25, -6.5) * mm});
            skLineSegment(sketch, "E315", {"start": v(-48.25, 0.02) * mm, "end": v(-45.63, 2.63) * mm});
            skLineSegment(sketch, "E316", {"start": v(-45.63, 2.63) * mm, "end": v(-48.25, 5.25) * mm});
            skLineSegment(sketch, "E317", {"start": v(-48.25, 5.25) * mm, "end": v(-48.25, 0.02) * mm});
            skLineSegment(sketch, "E318", {"start": v(-42.63, 5.63) * mm, "end": v(-40.02, 8.25) * mm});
            skLineSegment(sketch, "E319", {"start": v(-40.02, 8.25) * mm, "end": v(-45.25, 8.25) * mm});
            skLineSegment(sketch, "E320", {"start": v(-45.25, 8.25) * mm, "end": v(-42.63, 5.63) * mm});
            skLineSegment(sketch, "E321", {"start": v(-39.63, 2.63) * mm, "end": v(-37.02, 0.02) * mm});
            skLineSegment(sketch, "E322", {"start": v(-37.02, 0.02) * mm, "end": v(-37.02, 5.25) * mm});
            skLineSegment(sketch, "E323", {"start": v(-37.02, 5.25) * mm, "end": v(-39.63, 2.63) * mm});
            skLineSegment(sketch, "E324", {"start": v(-4.17, -17.25) * mm, "end": v(-9.37, -14.25) * mm});
            skLineSegment(sketch, "E325", {"start": v(-9.37, -14.25) * mm, "end": v(-11.76, -14.25) * mm});
            skLineSegment(sketch, "E326", {"start": v(-11.76, -14.25) * mm, "end": v(-8.76, -17.25) * mm});
            skLineSegment(sketch, "E327", {"start": v(-8.76, -17.25) * mm, "end": v(-4.17, -17.25) * mm});
            skSolve(sketch);
        }
        {
            var Q0;
            Q0 = qSketchRegion(id + "F25", true);
            extrude(context, id + "F26", {"entities" : qUnion([Q0]), "operationType" : NewBodyOperationType.ADD, "oppositeDirection" : true, "depth" : 2 * mm, "offsetDistance" : 25 * mm});
        }
        {
            var Q0;
            Q0=makeQuery(id+"F5.boolean.opBoolean","COPY",FACE,{"derivedFrom":makeQuery(id+"F5.opExtrude","SWEPT_FACE",FACE,{"disambiguationData":[OSD([sQuery(id+"F4.wireOp",EDGE,"E7")])]})});
            var sketch = newSketch(context, id + "F27", { "sketchPlane" : qUnion([Q0])});
            skLineSegment(sketch, "E328.0", {"start": v(30.25, 17) * mm, "end": v(30.25, 2) * mm});
            skLineSegment(sketch, "E328.1", {"start": v(32.25, 17) * mm, "end": v(30.25, 17) * mm});
            skLineSegment(sketch, "E328.2", {"start": v(32.25, 2) * mm, "end": v(32.25, 17) * mm});
            skLineSegment(sketch, "E328.3", {"start": v(30.25, 2) * mm, "end": v(32.25, 2) * mm});
            skSolve(sketch);
        }
        {
            var Q0;
            Q0 = qSketchRegion(id + "F27", true);
            extrude(context, id + "F28", {"entities" : qUnion([Q0]), "operationType" : NewBodyOperationType.ADD, "depth" : 1 * mm, "offsetDistance" : 25 * mm});
        }
        {
            var Q0;
            Q0=makeQuery(id+"F5.boolean.opBoolean","COPY",FACE,{"derivedFrom":makeQuery(id+"F5.opExtrude","SWEPT_FACE",FACE,{"disambiguationData":[OSD([sQuery(id+"F4.wireOp",EDGE,"E5")])]})});
            var sketch = newSketch(context, id + "F29", { "sketchPlane" : qUnion([Q0])});
            skLineSegment(sketch, "E329.0", {"start": v(-30.25, 17) * mm, "end": v(-32.25, 17) * mm});
            skLineSegment(sketch, "E329.1", {"start": v(-30.25, 2) * mm, "end": v(-30.25, 17) * mm});
            skLineSegment(sketch, "E329.2", {"start": v(-32.25, 2) * mm, "end": v(-30.25, 2) * mm});
            skLineSegment(sketch, "E329.3", {"start": v(-32.25, 17) * mm, "end": v(-32.25, 2) * mm});
            skSolve(sketch);
        }
        {
            var Q0;
            Q0 = qSketchRegion(id + "F29", true);
            extrude(context, id + "F30", {"entities" : qUnion([Q0]), "operationType" : NewBodyOperationType.ADD, "depth" : 1 * mm, "offsetDistance" : 25 * mm});
        }
        {
            var Q0;
            Q0=makeQuery(id+"F5.boolean.opBoolean","COPY",FACE,{"derivedFrom":makeQuery(id+"F5.opExtrude","SWEPT_FACE",FACE,{"disambiguationData":[OSD([sQuery(id+"F4.wireOp",EDGE,"E10.trimOffspring")])]})});
            var sketch = newSketch(context, id + "F31", { "sketchPlane" : qUnion([Q0])});
            skLineSegment(sketch, "E330.0", {"start": v(-70.25, 30.25) * mm, "end": v(-46.25, 30.25) * mm});
            skLineSegment(sketch, "E330.1", {"start": v(-70.25, 32.25) * mm, "end": v(-70.25, 30.25) * mm});
            skLineSegment(sketch, "E330.2", {"start": v(-46.25, 32.25) * mm, "end": v(-70.25, 32.25) * mm});
            skLineSegment(sketch, "E330.3", {"start": v(-46.25, 30.25) * mm, "end": v(-46.25, 32.25) * mm});
            skLineSegment(sketch, "E331.0", {"start": v(53.25, 32.25) * mm, "end": v(-43.25, 32.25) * mm});
            skLineSegment(sketch, "E331.1", {"start": v(53.25, 30.25) * mm, "end": v(53.25, 32.25) * mm});
            skLineSegment(sketch, "E331.2", {"start": v(-43.25, 30.25) * mm, "end": v(53.25, 30.25) * mm});
            skLineSegment(sketch, "E331.3", {"start": v(-43.25, 32.25) * mm, "end": v(-43.25, 30.25) * mm});
            skLineSegment(sketch, "E332.0", {"start": v(56.25, 30.25) * mm, "end": v(70.25, 30.25) * mm});
            skLineSegment(sketch, "E332.1", {"start": v(56.25, 32.25) * mm, "end": v(56.25, 30.25) * mm});
            skLineSegment(sketch, "E332.2", {"start": v(70.25, 32.25) * mm, "end": v(56.25, 32.25) * mm});
            skLineSegment(sketch, "E332.3", {"start": v(70.25, 30.25) * mm, "end": v(70.25, 32.25) * mm});
            skSolve(sketch);
        }
        {
            var Q0;
            Q0 = qSketchRegion(id + "F31", true);
            extrude(context, id + "F32", {"entities" : qUnion([Q0]), "operationType" : NewBodyOperationType.ADD, "depth" : 1 * mm, "offsetDistance" : 25 * mm});
        }
        {
            var Q0;
            {var subQ0=sQuery(id+"F0.wireOp",EDGE,"E0.top");var subQ1=sQuery(id+"F0.wireOp",EDGE,"E0.right");var subQ2=sQuery(id+"F0.wireOp",EDGE,"E0.bottom");var subQ3=sQuery(id+"F0.wireOp",EDGE,"E0.left");var subQ4=makeQuery(id+"F1.opExtrude","CAP_FACE",FACE,{"disambiguationData":[OSD([subQ2,subQ0,subQ3,subQ1])],"isStart":true});Q0=makeQuery(id+"F26.boolean.opBoolean","MERGE",FACE,{"derivedFrom":[makeQuery(id+"F20.opBoolean","MERGE",FACE,{"derivedFrom":[makeQuery(id+"F17.boolean.opBoolean","SPLIT",FACE,{"disambiguationData":[TD([makeQuery(id+"F17.opExtrude","SWEPT_FACE",FACE,{"disambiguationData":[OSD([sQuery(id+"F16.wireOp",EDGE,"E162.0")])]})])],"derivedFrom":subQ4}),makeQuery(id+"F17.boolean.opBoolean","SPLIT",FACE,{"disambiguationData":[TD([makeQuery(id+"F1.opExtrude","SWEPT_FACE",FACE,{"disambiguationData":[OSD([subQ2])]})])],"derivedFrom":subQ4}),makeQuery(id+"F19.opExtrude","CAP_FACE",FACE,{"disambiguationData":[OSD([sQuery(id+"F18.wireOp",EDGE,"E165.0"),sQuery(id+"F18.wireOp",EDGE,"E166.6"),sQuery(id+"F18.wireOp",EDGE,"E183"),sQuery(id+"F18.wireOp",EDGE,"E184")])],"isStart":true}),makeQuery(id+"F19.opExtrude","CAP_FACE",FACE,{"disambiguationData":[OSD([sQuery(id+"F18.wireOp",EDGE,"E165.1"),sQuery(id+"F18.wireOp",EDGE,"E166.5"),sQuery(id+"F18.wireOp",EDGE,"E181"),sQuery(id+"F18.wireOp",EDGE,"E182")])],"isStart":true}),makeQuery(id+"F19.opExtrude","CAP_FACE",FACE,{"disambiguationData":[OSD([sQuery(id+"F18.wireOp",EDGE,"E165.2"),sQuery(id+"F18.wireOp",EDGE,"E166.7"),sQuery(id+"F18.wireOp",EDGE,"E185"),sQuery(id+"F18.wireOp",EDGE,"E186")])],"isStart":true}),makeQuery(id+"F19.opExtrude","CAP_FACE",FACE,{"disambiguationData":[OSD([sQuery(id+"F18.wireOp",EDGE,"E165.3"),sQuery(id+"F18.wireOp",EDGE,"E166.4"),sQuery(id+"F18.wireOp",EDGE,"E171"),sQuery(id+"F18.wireOp",EDGE,"E172")])],"isStart":true}),makeQuery(id+"F19.opExtrude","CAP_FACE",FACE,{"disambiguationData":[OSD([sQuery(id+"F18.wireOp",EDGE,"E165.4"),sQuery(id+"F18.wireOp",EDGE,"E166.3"),sQuery(id+"F18.wireOp",EDGE,"E168"),sQuery(id+"F18.wireOp",EDGE,"E169")])],"isStart":true}),makeQuery(id+"F19.opExtrude","CAP_FACE",FACE,{"disambiguationData":[OSD([sQuery(id+"F18.wireOp",EDGE,"E165.5"),sQuery(id+"F18.wireOp",EDGE,"E166.1"),sQuery(id+"F18.wireOp",EDGE,"E187"),sQuery(id+"F18.wireOp",EDGE,"E188")])],"isStart":true}),makeQuery(id+"F19.opExtrude","CAP_FACE",FACE,{"disambiguationData":[OSD([sQuery(id+"F18.wireOp",EDGE,"E165.6"),sQuery(id+"F18.wireOp",EDGE,"E166.0"),sQuery(id+"F18.wireOp",EDGE,"E178"),sQuery(id+"F18.wireOp",EDGE,"E189")])],"isStart":true}),makeQuery(id+"F19.opExtrude","CAP_FACE",FACE,{"disambiguationData":[OSD([sQuery(id+"F18.wireOp",EDGE,"E165.7"),sQuery(id+"F18.wireOp",EDGE,"E166.2"),sQuery(id+"F18.wireOp",EDGE,"E179"),sQuery(id+"F18.wireOp",EDGE,"E180")])],"isStart":true})]}),makeQuery(id+"F26.opExtrude","CAP_FACE",FACE,{"disambiguationData":[OSD([sQuery(id+"F25.wireOp",EDGE,"E298"),sQuery(id+"F25.wireOp",EDGE,"E299"),sQuery(id+"F25.wireOp",EDGE,"E300"),sQuery(id+"F25.wireOp",EDGE,"E304")])],"isStart":true}),makeQuery(id+"F26.opExtrude","CAP_FACE",FACE,{"disambiguationData":[OSD([sQuery(id+"F25.wireOp",EDGE,"E301"),sQuery(id+"F25.wireOp",EDGE,"E302"),sQuery(id+"F25.wireOp",EDGE,"E303"),sQuery(id+"F25.wireOp",EDGE,"E305")])],"isStart":true}),makeQuery(id+"F26.opExtrude","CAP_FACE",FACE,{"disambiguationData":[OSD([sQuery(id+"F25.wireOp",EDGE,"E306"),sQuery(id+"F25.wireOp",EDGE,"E307"),sQuery(id+"F25.wireOp",EDGE,"E308")])],"isStart":true}),makeQuery(id+"F26.opExtrude","CAP_FACE",FACE,{"disambiguationData":[OSD([sQuery(id+"F25.wireOp",EDGE,"E309"),sQuery(id+"F25.wireOp",EDGE,"E310"),sQuery(id+"F25.wireOp",EDGE,"E311")])],"isStart":true}),makeQuery(id+"F26.opExtrude","CAP_FACE",FACE,{"disambiguationData":[OSD([sQuery(id+"F25.wireOp",EDGE,"E312"),sQuery(id+"F25.wireOp",EDGE,"E313"),sQuery(id+"F25.wireOp",EDGE,"E314")])],"isStart":true}),makeQuery(id+"F26.opExtrude","CAP_FACE",FACE,{"disambiguationData":[OSD([sQuery(id+"F25.wireOp",EDGE,"E315"),sQuery(id+"F25.wireOp",EDGE,"E316"),sQuery(id+"F25.wireOp",EDGE,"E317")])],"isStart":true}),makeQuery(id+"F26.opExtrude","CAP_FACE",FACE,{"disambiguationData":[OSD([sQuery(id+"F25.wireOp",EDGE,"E318"),sQuery(id+"F25.wireOp",EDGE,"E319"),sQuery(id+"F25.wireOp",EDGE,"E320")])],"isStart":true}),makeQuery(id+"F26.opExtrude","CAP_FACE",FACE,{"disambiguationData":[OSD([sQuery(id+"F25.wireOp",EDGE,"E321"),sQuery(id+"F25.wireOp",EDGE,"E322"),sQuery(id+"F25.wireOp",EDGE,"E323")])],"isStart":true}),makeQuery(id+"F26.opExtrude","CAP_FACE",FACE,{"disambiguationData":[OSD([sQuery(id+"F25.wireOp",EDGE,"E324"),sQuery(id+"F25.wireOp",EDGE,"E325"),sQuery(id+"F25.wireOp",EDGE,"E326"),sQuery(id+"F25.wireOp",EDGE,"E327")])],"isStart":true})]});}
            var sketch = newSketch(context, id + "F33", { "sketchPlane" : qUnion([Q0])});
            skLineSegment(sketch, "E333", {"start": v(-51.25, 14.25) * mm, "end": v(-34.02, 14.25) * mm});
            skLineSegment(sketch, "E334", {"start": v(-34.02, 14.25) * mm, "end": v(-31.02, 11.25) * mm});
            skLineSegment(sketch, "E335", {"start": v(-31.02, 11.25) * mm, "end": v(-31.02, -12.25) * mm});
            skLineSegment(sketch, "E336", {"start": v(-31.02, -12.25) * mm, "end": v(-34.02, -15.25) * mm});
            skLineSegment(sketch, "E337", {"start": v(-34.02, -15.25) * mm, "end": v(-51.25, -15.25) * mm});
            skLineSegment(sketch, "E338", {"start": v(-51.25, -15.25) * mm, "end": v(-54.25, -12.25) * mm});
            skLineSegment(sketch, "E339", {"start": v(-54.25, -12.25) * mm, "end": v(-54.25, 11.25) * mm});
            skLineSegment(sketch, "E340", {"start": v(-54.25, 11.25) * mm, "end": v(-51.25, 14.25) * mm});
            skSolve(sketch);
        }
        {
            var Q0;
            Q0 = qSketchRegion(id + "F33", true);
            extrude(context, id + "F34", {"entities" : qUnion([Q0]), "operationType" : NewBodyOperationType.REMOVE, "oppositeDirection" : true, "depth" : 2 * mm, "offsetDistance" : 25 * mm});
        }
    });
